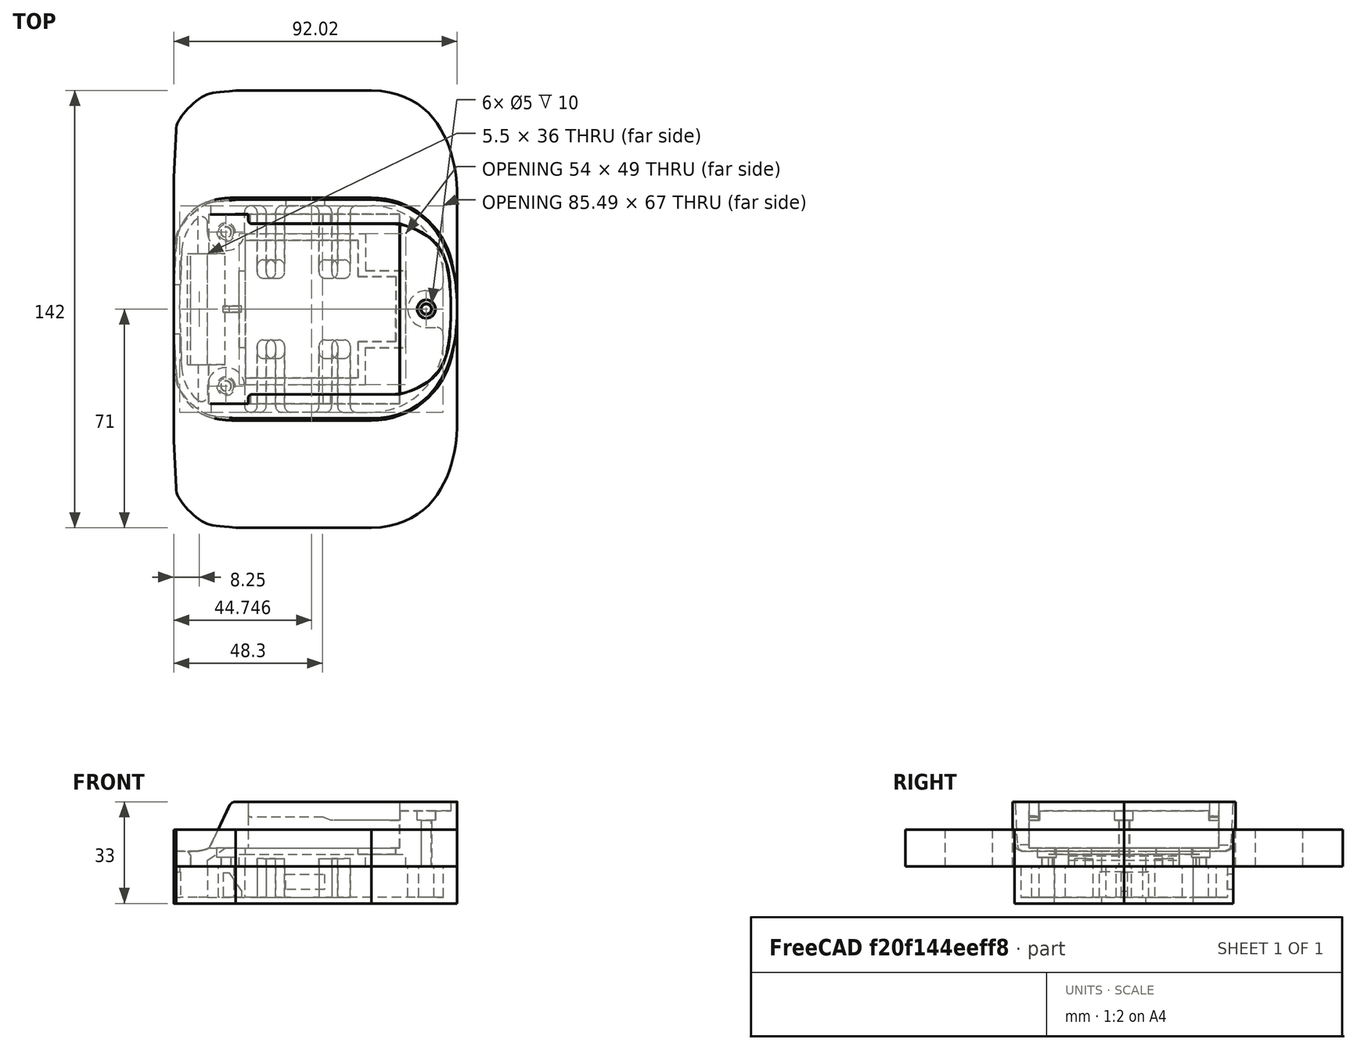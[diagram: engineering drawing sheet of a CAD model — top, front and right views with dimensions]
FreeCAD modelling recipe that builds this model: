
FCSTD DOCUMENT  (FreeCAD 1.0R39319 (Git))
Label: Makita LXT  - 18V - Battery holder
License: Creative Commons Attribution 4.0
LicenseURL: https://creativecommons.org/licenses/by/4.0/
objects: Sketcher::SketchObject×30, PartDesign::Pocket×23, TechDraw::DrawViewDimension×9, PartDesign::Pad×7, PartDesign::Body×5, TechDraw::DrawProjGroupItem×3, PartDesign::Mirrored×3, TechDraw::DrawSVGTemplate×2, TechDraw::DrawPage×2, Mesh::Feature×1, Part::Feature×1, TechDraw::DrawProjGroup×1
note: 180 computed .brp shape members not serialized (recipe doc carries the construction recipe); baked Part::Feature solids carry a one-line shape summary decoded from their .brp

FEATURE [Sketcher::SketchObject] Sketch
  ArcFitTolerance = 0
  AttachmentSupport = -> [XY_Plane]
  FullyConstrained = false
  MakeInternals = false
  MapMode = 5
  sketch-geometry (26):
    g0: ArcOfCircle CenterX=259.65 CenterY=-2.5774e-06 CenterZ=0 NormalX=0 NormalY=0 NormalZ=1 AngleXU=0 Radius=259.65 StartAngle=3.05831 EndAngle=3.14159
    g1: ArcOfCircle CenterX=16.3351 CenterY=20.3115 CenterZ=0 NormalX=0 NormalY=0 NormalZ=1 AngleXU=0 Radius=15.4888 StartAngle=1.76803 EndAngle=3.05831
    g2: LineSegment StartX=20 StartY=36.1629 StartZ=0 EndX=64.2 EndY=36.1629 EndZ=0
    g3: ArcOfCircle CenterX=64.2 CenterY=9.3939 CenterZ=0 NormalX=0 NormalY=0 NormalZ=1 AngleXU=0 Radius=26.769 StartAngle=0.218634 EndAngle=1.5708
    g4: ArcOfCircle CenterX=21.9206 CenterY=0 CenterZ=0 NormalX=0 NormalY=0 NormalZ=1 AngleXU=0 Radius=70.0794 StartAngle=0 EndAngle=0.218634
    g5: ArcOfCircle CenterX=20 CenterY=1.97116 CenterZ=0 NormalX=0 NormalY=0 NormalZ=1 AngleXU=0 Radius=34.1917 StartAngle=1.5708 EndAngle=1.76803
    g6: Circle CenterX=17 CenterY=25 CenterZ=0 NormalX=0 NormalY=0 NormalZ=1 AngleXU=0 Radius=1.6
    g7: ArcOfCircle CenterX=82 CenterY=0 CenterZ=0 NormalX=0 NormalY=0 NormalZ=1 AngleXU=0 Radius=1.6 StartAngle=0 EndAngle=3.14159
    g8: LineSegment StartX=23.3 StartY=0 StartZ=0 EndX=23.3 EndY=22.4 EndZ=0
    g9: LineSegment StartX=23.3 StartY=22.4 StartZ=0 EndX=59.9 EndY=22.4 EndZ=0
    g10: LineSegment StartX=59.9 StartY=22.4 StartZ=0 EndX=59.9 EndY=10.5 EndZ=0
    g11: LineSegment StartX=59.9 StartY=10.5 StartZ=0 EndX=72.1 EndY=10.5 EndZ=0
    g12: LineSegment StartX=72.1 StartY=10.5 StartZ=0 EndX=72.1 EndY=0 EndZ=0
    g13: ArcOfCircle CenterX=259.65 CenterY=2.5774e-06 CenterZ=0 NormalX=0 NormalY=0 NormalZ=1 AngleXU=0 Radius=259.65 StartAngle=3.14159 EndAngle=3.22488
    g14: ArcOfCircle CenterX=16.3351 CenterY=-20.3115 CenterZ=0 NormalX=0 NormalY=0 NormalZ=1 AngleXU=0 Radius=15.4888 StartAngle=3.22488 EndAngle=4.51516
    g15: LineSegment StartX=20 StartY=-36.1629 StartZ=0 EndX=64.2 EndY=-36.1629 EndZ=0
    g16: ArcOfCircle CenterX=64.2 CenterY=-9.3939 CenterZ=0 NormalX=0 NormalY=0 NormalZ=1 AngleXU=0 Radius=26.769 StartAngle=4.71239 EndAngle=6.06455
    g17: ArcOfCircle CenterX=21.9206 CenterY=0 CenterZ=0 NormalX=0 NormalY=0 NormalZ=1 AngleXU=0 Radius=70.0794 StartAngle=6.06455 EndAngle=6.28319
    g18: ArcOfCircle CenterX=20 CenterY=-1.97116 CenterZ=0 NormalX=0 NormalY=0 NormalZ=1 AngleXU=0 Radius=34.1917 StartAngle=4.51516 EndAngle=4.71239
    g19: Circle CenterX=17 CenterY=-25 CenterZ=0 NormalX=0 NormalY=0 NormalZ=1 AngleXU=0 Radius=1.6
    g20: ArcOfCircle CenterX=82 CenterY=0 CenterZ=0 NormalX=0 NormalY=0 NormalZ=1 AngleXU=0 Radius=1.6 StartAngle=3.14159 EndAngle=6.28319
    g21: LineSegment StartX=23.3 StartY=0 StartZ=0 EndX=23.3 EndY=-22.4 EndZ=0
    g22: LineSegment StartX=23.3 StartY=-22.4 StartZ=0 EndX=59.9 EndY=-22.4 EndZ=0
    g23: LineSegment StartX=59.9 StartY=-22.4 StartZ=0 EndX=59.9 EndY=-10.5 EndZ=0
    g24: LineSegment StartX=59.9 StartY=-10.5 StartZ=0 EndX=72.1 EndY=-10.5 EndZ=0
    g25: LineSegment StartX=72.1 StartY=-10.5 StartZ=0 EndX=72.1 EndY=0 EndZ=0
  constraints (64):
    c: Horizontal(g2)
    c: DistanceX(g2) = 20
    c: DistanceX(g2,g2) = 44.2
    c: Tangent(g4,g3) = -1.5708
    c: Tangent(g3,g2) = 1.5708
    c: Tangent(g1,g0) = -1.5708
    c: Tangent(g5,g2) = 1.5708
    c: Tangent(g5,g1) = -1.5708
    c: DistanceX(g0) = 0.9
    c: DistanceX(g1) = 13.3
    c: DistanceX(g4) = 92
    c: Coincident(g0,g-1)
    c: DistanceY(g0) = 21.6
    c: DistanceY(g1) = 35.5
    c: PointOnObject(g4,g-1)
    c: DistanceY(g3) = 15.2
    c: DistanceY(g6) = 25
    c: DistanceX(g6) = 17
    c: Diameter(g6) = 3.2
    c: PointOnObject(g7,g-1)
    c: PointOnObject(g7,g-1)
    c: PointOnObject(g7,g-1)
    c: DistanceX(g6,g7) = 65
    c: Equal(g7,g6)
    c: Tangent(g0,g-2)
    c: Perpendicular(g4,g-1)
    c: PointOnObject(g8,g-1)
    c: Vertical(g8)
    c: Coincident(g8,g9)
    c: Horizontal(g9)
    c: Coincident(g9,g10)
    c: Vertical(g10)
    c: Coincident(g10,g11)
    c: Horizontal(g11)
    c: Coincident(g11,g12)
    c: Vertical(g12)
    c: DistanceX(g8) = 23.3
    c: DistanceY(g8) = 22.4
    c: DistanceX(g9,g9) = 36.6
    c: DistanceY(g10,g10) = 11.9
    c: DistanceX(g11,g11) = 12.2
    c: PointOnObject(g12,g-1)
    c: Horizontal(g15)
    c: Tangent(g17,g16) = -1.5708
    c: Tangent(g16,g15) = -1.5708
    c: Tangent(g14,g13) = -1.5708
    c: Tangent(g18,g15) = -1.5708
    c: Tangent(g18,g14) = -1.5708
    c: Diameter(g19) = 3.2
    c: Equal(g20,g19)
    c: Vertical(g21)
    c: Coincident(g21,g22)
    c: Horizontal(g22)
    c: Coincident(g22,g23)
    c: Vertical(g23)
    c: Coincident(g23,g24)
    c: Horizontal(g24)
    c: Coincident(g24,g25)
    c: Vertical(g25)
    c: DistanceY(g15,g2) = 72.3257
    c: DistanceY(g19,g6) = 50
    c: DistanceX(g6,g7) = 66.6
    c: DistanceX(g6) = 17
    c: DistanceX(g4) = 92
FEATURE [Mesh::Feature] Makita_18V_Body  label="Makita 18V-Body"
  Placement = pos=(17,0,0) rot=(0,0,1;0rad)
FEATURE [PartDesign::Pad] Pad
  Direction = (0,0,1)
  Length = 21
  Length2 = 10
  Profile = -> Sketch
  ReferenceAxis = -> Sketch [N_Axis]
  Suppressed = false
  Type = 0
FEATURE [Sketcher::SketchObject] Sketch001
  ArcFitTolerance = 0
  AttachmentSupport = -> [XZ_Plane]
  FullyConstrained = true
  MakeInternals = false
  MapMode = 5
  Placement = pos=(0,0,0) rot=(1,0,0;1.5708rad)
  sketch-geometry (8):
    g0: LineSegment StartX=0 StartY=5 StartZ=0 EndX=0 EndY=21 EndZ=0
    g1: LineSegment StartX=0 StartY=21 StartZ=0 EndX=20 EndY=21 EndZ=0
    g2: LineSegment StartX=0 StartY=5 StartZ=0 EndX=7.9 EndY=5 EndZ=0
    g3: LineSegment StartX=18.2 StartY=19.8659 StartZ=0 EndX=11.9 EndY=6.7 EndZ=0
    g4: ArcOfCircle CenterX=20 CenterY=19.0045 CenterZ=0 NormalX=0 NormalY=0 NormalZ=1 AngleXU=0 Radius=1.99546 StartAngle=1.5708 EndAngle=2.69528
    g5: ArcOfCircle CenterX=10.0257 CenterY=7.59685 CenterZ=0 NormalX=0 NormalY=0 NormalZ=1 AngleXU=0 Radius=2.07779 StartAngle=4.99242 EndAngle=5.83688
    g6: ArcOfCircle CenterX=7.9 CenterY=5.60003 CenterZ=0 NormalX=0 NormalY=0 NormalZ=1 AngleXU=0 Radius=0.600034 StartAngle=4.71239 EndAngle=4.87983
    g7: ArcOfCircle CenterX=4.0509 CenterY=28.3729 CenterZ=0 NormalX=0 NormalY=0 NormalZ=1 AngleXU=0 Radius=23.6959 StartAngle=4.87983 EndAngle=4.99242
  constraints (22):
    c: PointOnObject(g0,g-2)
    c: PointOnObject(g0,g-2)
    c: Horizontal(g1)
    c: Coincident(g1,g0)
    c: DistanceY(g0) = 5
    c: DistanceY(g0) = 21
    c: Coincident(g2,g0)
    c: Horizontal(g2)
    c: Tangent(g4,g3) = -1.5708
    c: Tangent(g5,g3) = 1.5708
    c: Tangent(g4,g1) = 1.5708
    c: DistanceX(g1,g1) = 20
    c: DistanceX(g3) = 11.9
    c: DistanceY(g3) = 6.7
    c: DistanceX(g3) = 18.2
    c: Tangent(g6,g2) = -1.5708
    c: DistanceX(g2,g2) = 7.9
    c: Tangent(g7,g5) = -1.5708
    c: Tangent(g7,g6) = -1.5708
    c: DistanceX(g2,g6) = 0.1
    c: DistanceX(g5) = 10.6
    c: DistanceY(g5) = 5.6
FEATURE [PartDesign::Pocket] Pocket
  BaseFeature = -> Pad
  Direction = (0,1,-2e-16)
  Length = 5
  Length2 = 5
  Midplane = true
  Profile = -> Sketch001
  ReferenceAxis = -> Sketch001 [N_Axis]
  Suppressed = false
  Type = 1
FEATURE [Part::Feature] Makita_18V_Body001
  shape: bbox 92 x 71 x 21 mm, 5406 faces, 0 solids (baked)
FEATURE [Sketcher::SketchObject] Sketch002
  ArcFitTolerance = 0
  AttachmentSupport = -> [Pocket]
  FullyConstrained = false
  MakeInternals = false
  MapMode = 5
  Placement = pos=(0,0,21) rot=(0,0,1;0rad)
  sketch-geometry (16):
    g0: LineSegment StartX=24.2 StartY=30.78 StartZ=0 EndX=0 EndY=30.78 EndZ=0
    g1: LineSegment StartX=24.2 StartY=30.78 StartZ=0 EndX=24.2 EndY=28.88 EndZ=0
    g2: LineSegment StartX=25.4 StartY=27.68 StartZ=0 EndX=70.2 EndY=27.68 EndZ=0
    g3: ArcOfCircle CenterX=25.4 CenterY=28.88 CenterZ=0 NormalX=0 NormalY=0 NormalZ=1 AngleXU=0 Radius=1.2 StartAngle=3.14159 EndAngle=4.71239
    g4: ArcOfCircle CenterX=15.7361 CenterY=0 CenterZ=0 NormalX=0 NormalY=0 NormalZ=1 AngleXU=0 Radius=74.2639 StartAngle=0 EndAngle=0.199259
    g5: ArcOfCircle CenterX=74.666 CenterY=11.9002 CenterZ=0 NormalX=0 NormalY=0 NormalZ=1 AngleXU=0 Radius=14.1444 StartAngle=0.199259 EndAngle=0.868771
    g6: ArcOfCircle CenterX=70.2 CenterY=6.61972 CenterZ=0 NormalX=0 NormalY=0 NormalZ=1 AngleXU=0 Radius=21.0603 StartAngle=0.868771 EndAngle=1.5708
    g7: LineSegment StartX=0 StartY=0 StartZ=0 EndX=0 EndY=30.78 EndZ=0
    g8: LineSegment StartX=24.2 StartY=-30.78 StartZ=0 EndX=0 EndY=-30.78 EndZ=0
    g9: LineSegment StartX=24.2 StartY=-30.78 StartZ=0 EndX=24.2 EndY=-28.88 EndZ=0
    g10: LineSegment StartX=25.4 StartY=-27.68 StartZ=0 EndX=70.2 EndY=-27.68 EndZ=0
    g11: ArcOfCircle CenterX=25.4 CenterY=-28.88 CenterZ=0 NormalX=0 NormalY=0 NormalZ=1 AngleXU=0 Radius=1.2 StartAngle=1.5708 EndAngle=3.14159
    g12: ArcOfCircle CenterX=15.7361 CenterY=0 CenterZ=0 NormalX=0 NormalY=0 NormalZ=1 AngleXU=0 Radius=74.2639 StartAngle=6.08393 EndAngle=6.28319
    g13: ArcOfCircle CenterX=74.666 CenterY=-11.9002 CenterZ=0 NormalX=0 NormalY=0 NormalZ=1 AngleXU=0 Radius=14.1444 StartAngle=5.41441 EndAngle=6.08393
    g14: ArcOfCircle CenterX=70.2 CenterY=-6.61972 CenterZ=0 NormalX=0 NormalY=0 NormalZ=1 AngleXU=0 Radius=21.0603 StartAngle=4.71239 EndAngle=5.41441
    g15: LineSegment StartX=0 StartY=0 StartZ=0 EndX=0 EndY=-30.78 EndZ=0
  constraints (36):
    c: PointOnObject(g0,g-2)
    c: Horizontal(g0)
    c: DistanceY(g0) = 30.78
    c: DistanceX(g0,g0) = 24.2
    c: Coincident(g1,g0)
    c: Vertical(g1)
    c: Horizontal(g2)
    c: Tangent(g3,g1) = -1.5708
    c: Tangent(g3,g2) = -1.5708
    c: DistanceY(g1,g1) = 1.9
    c: Radius(g3) = 1.2
    c: PointOnObject(g4,g-1)
    c: Perpendicular(g4,g-1)
    c: DistanceX(g4) = 90
    c: DistanceY(g4) = 14.7
    c: Tangent(g6,g5) = -1.5708
    c: Tangent(g5,g4) = -1.5708
    c: Tangent(g6,g2) = 1.5708
    c: DistanceX(g2,g2) = 44.8
    c: DistanceX(g5) = 83.8
    c: DistanceY(g5) = 22.7
    c: PointOnObject(g7,g-1)
    c: Coincident(g7,g0)
    c: Vertical(g7)
    c: Horizontal(g8)
    c: Coincident(g9,g8)
    c: Vertical(g9)
    c: Horizontal(g10)
    c: Tangent(g11,g9) = 1.5708
    c: Tangent(g11,g10) = 1.5708
    c: Radius(g11) = 1.2
    c: Tangent(g14,g13) = -1.5708
    c: Tangent(g13,g12) = -1.5708
    c: Tangent(g14,g10) = -1.5708
    c: Coincident(g15,g8)
    c: Vertical(g15)
FEATURE [PartDesign::Pocket] Pocket001
  BaseFeature = -> Pocket
  Direction = (0,0,-1)
  Length = 3
  Length2 = 5
  Profile = -> Sketch002
  ReferenceAxis = -> Sketch002 [N_Axis]
  Suppressed = false
  Type = 0
FEATURE [Sketcher::SketchObject] Sketch003
  ArcFitTolerance = 0
  AttachmentSupport = -> [Pocket001]
  ExternalGeometry = -> [Sketch002]
  FullyConstrained = false
  MakeInternals = false
  MapMode = 5
  Placement = pos=(0,0,18) rot=(0,0,1;0rad)
  sketch-geometry (14):
    g0: LineSegment StartX=0 StartY=0 StartZ=0 EndX=0 EndY=30.78 EndZ=0
    g1: LineSegment StartX=0 StartY=30.78 StartZ=0 EndX=24.2 EndY=30.78 EndZ=0
    g2: LineSegment StartX=24.2 StartY=28.88 StartZ=0 EndX=24.2 EndY=30.78 EndZ=0
    g3: LineSegment StartX=25.4 StartY=27.68 StartZ=0 EndX=70.2 EndY=27.68 EndZ=0
    g4: ArcOfCircle CenterX=25.4 CenterY=28.88 CenterZ=0 NormalX=0 NormalY=0 NormalZ=1 AngleXU=0 Radius=1.2 StartAngle=3.14159 EndAngle=4.71239
    g5: LineSegment StartX=73.4 StartY=27.4355 StartZ=0 EndX=73.4 EndY=0 EndZ=0
    g6: ArcOfCircle CenterX=70.2 CenterY=6.61972 CenterZ=0 NormalX=0 NormalY=0 NormalZ=1 AngleXU=0 Radius=21.0603 StartAngle=1.41826 EndAngle=1.5708
    g7: LineSegment StartX=0 StartY=0 StartZ=0 EndX=0 EndY=-30.78 EndZ=0
    g8: LineSegment StartX=0 StartY=-30.78 StartZ=0 EndX=24.2 EndY=-30.78 EndZ=0
    g9: LineSegment StartX=24.2 StartY=-28.88 StartZ=0 EndX=24.2 EndY=-30.78 EndZ=0
    g10: LineSegment StartX=25.4 StartY=-27.68 StartZ=0 EndX=70.2 EndY=-27.68 EndZ=0
    g11: ArcOfCircle CenterX=25.4 CenterY=-28.88 CenterZ=0 NormalX=0 NormalY=0 NormalZ=1 AngleXU=0 Radius=1.2 StartAngle=1.5708 EndAngle=3.14159
    g12: LineSegment StartX=73.4 StartY=-27.4355 StartZ=0 EndX=73.4 EndY=0 EndZ=0
    g13: ArcOfCircle CenterX=70.2 CenterY=-6.61972 CenterZ=0 NormalX=0 NormalY=0 NormalZ=1 AngleXU=0 Radius=21.0603 StartAngle=4.71239 EndAngle=4.86492
  constraints (23):
    c: Coincident(g0,g-3)
    c: Coincident(g0,g-4)
    c: Coincident(g1,g0)
    c: Coincident(g1,g-4)
    c: Coincident(g2,g-7)
    c: Coincident(g2,g1)
    c: Coincident(g3,g-5)
    c: Coincident(g3,g-6)
    c: Coincident(g4,g2)
    c: Tangent(g4,g3) = -1.5708
    c: PointOnObject(g5,g-6)
    c: PointOnObject(g5,g-1)
    c: Vertical(g5)
    c: Coincident(g6,g5)
    c: Tangent(g6,g3) = 1.5708
    c: DistanceX(g5) = 73.4
    c: Coincident(g8,g7)
    c: Coincident(g9,g8)
    c: Coincident(g11,g9)
    c: Tangent(g11,g10) = 1.5708
    c: Vertical(g12)
    c: Coincident(g13,g12)
    c: Tangent(g13,g10) = -1.5708
FEATURE [PartDesign::Pocket] Pocket002
  BaseFeature = -> Pocket001
  Direction = (0,0,-1)
  Length = 12
  Length2 = 5
  Profile = -> Sketch003
  ReferenceAxis = -> Sketch003 [N_Axis]
  Suppressed = false
  Type = 0
FEATURE [Sketcher::SketchObject] Sketch004
  ArcFitTolerance = 0
  AttachmentSupport = -> [Pocket002]
  ExternalGeometry = -> [Pocket002]
  FullyConstrained = true
  MakeInternals = false
  MapMode = 5
  Placement = pos=(0,0,6) rot=(0,0,1;0rad)
  sketch-geometry (2):
    g0: Circle CenterX=17 CenterY=25 CenterZ=0 NormalX=0 NormalY=0 NormalZ=1 AngleXU=0 Radius=3
    g1: Circle CenterX=17 CenterY=-25 CenterZ=0 NormalX=0 NormalY=0 NormalZ=1 AngleXU=0 Radius=3
  constraints (4):
    c: Symmetric(g1,g0,g-1)
    c: Equal(g0,g1)
    c: Coincident(g-3,g0)
    c: Diameter(g0) = 6
FEATURE [PartDesign::Pocket] Pocket003
  BaseFeature = -> Pocket002
  Direction = (0,0,-1)
  Length = 3
  Length2 = 5
  Profile = -> Sketch004
  ReferenceAxis = -> Sketch004 [N_Axis]
  Suppressed = false
  Type = 0
FEATURE [Sketcher::SketchObject] Sketch005
  ArcFitTolerance = 0
  AttachmentSupport = -> [Pocket003]
  ExternalGeometry = -> [Pocket003]
  FullyConstrained = true
  MakeInternals = false
  MapMode = 5
  Placement = pos=(0,0,18) rot=(0,0,1;0rad)
  sketch-geometry (1):
    g0: Circle CenterX=82 CenterY=0 CenterZ=0 NormalX=0 NormalY=0 NormalZ=1 AngleXU=0 Radius=3
  constraints (2):
    c: Coincident(g0,g-3)
    c: Diameter(g0) = 6
FEATURE [PartDesign::Pocket] Pocket004
  BaseFeature = -> Pocket003
  Direction = (0,0,-1)
  Length = 3
  Length2 = 5
  Profile = -> Sketch005
  ReferenceAxis = -> Sketch005 [N_Axis]
  Suppressed = false
  Type = 0
FEATURE [Sketcher::SketchObject] Sketch006
  ArcFitTolerance = 0
  AttachmentSupport = -> [XZ_Plane]
  ExternalGeometry = -> [Sketch003]
  FullyConstrained = true
  MakeInternals = false
  MapMode = 5
  Placement = pos=(0,0,0) rot=(1,0,0;1.5708rad)
  sketch-geometry (7):
    g0: LineSegment StartX=73.4 StartY=15 StartZ=0 EndX=51 EndY=15 EndZ=0
    g1: LineSegment StartX=51 StartY=15 StartZ=0 EndX=48.5 EndY=16 EndZ=0
    g2: LineSegment StartX=48.5 StartY=16 StartZ=0 EndX=25 EndY=16 EndZ=0
    g3: LineSegment StartX=24.2 StartY=16.4 StartZ=0 EndX=25 EndY=16 EndZ=0
    g4: LineSegment StartX=24.2 StartY=16.4 StartZ=0 EndX=24.2 EndY=6 EndZ=0
    g5: LineSegment StartX=24.2 StartY=6 StartZ=0 EndX=73.4 EndY=6 EndZ=0
    g6: LineSegment StartX=73.4 StartY=6 StartZ=0 EndX=73.4 EndY=15 EndZ=0
  constraints (21):
    c: Horizontal(g0)
    c: Coincident(g1,g0)
    c: Coincident(g2,g1)
    c: Horizontal(g2)
    c: Coincident(g2,g3)
    c: Coincident(g4,g3)
    c: Vertical(g4)
    c: Coincident(g5,g4)
    c: Horizontal(g5)
    c: Coincident(g6,g5)
    c: Coincident(g6,g0)
    c: Vertical(g6)
    c: Vertical(g0,g-3)
    c: Vertical(g3,g-5)
    c: DistanceY(g4) = 6
    c: DistanceY(g4,g4) = 10.4
    c: DistanceY(g2) = 16
    c: DistanceX(g3,g2) = 0.8
    c: DistanceX(g2,g2) = 23.5
    c: DistanceY(g0) = 15
    c: DistanceX(g1,g0) = 2.5
FEATURE [PartDesign::Pocket] Pocket005
  BaseFeature = -> Pocket004
  Direction = (0,1,-2e-16)
  Length = 61.6
  Length2 = 5
  Midplane = true
  Profile = -> Sketch006
  ReferenceAxis = -> Sketch006 [N_Axis]
  Suppressed = false
  Type = 0
FEATURE [Sketcher::SketchObject] Sketch007
  ArcFitTolerance = 0
  AttachmentSupport = -> [Pocket005]
  ExternalGeometry = -> [Pocket005]
  FullyConstrained = false
  MakeInternals = false
  MapMode = 5
  Placement = pos=(0,0,0) rot=(1,0,0;3.14159rad)
  sketch-geometry (14):
    g0: LineSegment StartX=21.3 StartY=0 StartZ=0 EndX=21.3 EndY=12.5 EndZ=0
    g1: LineSegment StartX=21.3 StartY=12.5 StartZ=0 EndX=23.3 EndY=12.5 EndZ=0
    g2: LineSegment StartX=23.3 StartY=12.5 StartZ=0 EndX=23.3 EndY=24.5 EndZ=0
    g3: LineSegment StartX=23.3 StartY=24.5 StartZ=0 EndX=62.3 EndY=24.5 EndZ=0
    g4: LineSegment StartX=62.3 StartY=24.5 StartZ=0 EndX=62.3 EndY=12.5 EndZ=0
    g5: LineSegment StartX=62.3 StartY=12.5 StartZ=0 EndX=75.3 EndY=12.5 EndZ=0
    g6: LineSegment StartX=75.3 StartY=12.5 StartZ=0 EndX=75.3 EndY=0 EndZ=0
    g7: LineSegment StartX=21.3 StartY=0 StartZ=0 EndX=21.3 EndY=-12.5 EndZ=0
    g8: LineSegment StartX=21.3 StartY=-12.5 StartZ=0 EndX=23.3 EndY=-12.5 EndZ=0
    g9: LineSegment StartX=23.3 StartY=-12.5 StartZ=0 EndX=23.3 EndY=-24.5 EndZ=0
    g10: LineSegment StartX=23.3 StartY=-24.5 StartZ=0 EndX=62.3 EndY=-24.5 EndZ=0
    g11: LineSegment StartX=62.3 StartY=-24.5 StartZ=0 EndX=62.3 EndY=-12.5 EndZ=0
    g12: LineSegment StartX=62.3 StartY=-12.5 StartZ=0 EndX=75.3 EndY=-12.5 EndZ=0
    g13: LineSegment StartX=75.3 StartY=-12.5 StartZ=0 EndX=75.3 EndY=0 EndZ=0
  constraints (35):
    c: PointOnObject(g0,g-1)
    c: Vertical(g0)
    c: Coincident(g0,g1)
    c: PointOnObject(g1,g-3)
    c: Horizontal(g1)
    c: Coincident(g1,g2)
    c: Vertical(g2)
    c: Coincident(g2,g3)
    c: Horizontal(g3)
    c: Coincident(g3,g4)
    c: Vertical(g4)
    c: Coincident(g4,g5)
    c: Horizontal(g5)
    c: Coincident(g5,g6)
    c: PointOnObject(g6,g-1)
    c: Vertical(g6)
    c: DistanceY(g2) = 24.5
    c: DistanceY(g0,g0) = 12.5
    c: DistanceX(g1,g1) = 2
    c: DistanceX(g-4,g3) = 2.4
    c: DistanceY(g-5,g4) = 2
    c: DistanceX(g-5,g5) = 3.2
    c: Vertical(g7)
    c: Coincident(g7,g8)
    c: Horizontal(g8)
    c: Coincident(g8,g9)
    c: Vertical(g9)
    c: Coincident(g9,g10)
    c: Horizontal(g10)
    c: Coincident(g10,g11)
    c: Vertical(g11)
    c: Coincident(g11,g12)
    c: Horizontal(g12)
    c: Coincident(g12,g13)
    c: Vertical(g13)
FEATURE [PartDesign::Pocket] Pocket006
  BaseFeature = -> Pocket005
  Direction = (0,0,1)
  Length = 4
  Length2 = 5
  Profile = -> Sketch007
  ReferenceAxis = -> Sketch007 [N_Axis]
  Suppressed = false
  Type = 0
FEATURE [Sketcher::SketchObject] Sketch008
  ArcFitTolerance = 0
  AttachmentSupport = -> [XZ_Plane]
  FullyConstrained = true
  MakeInternals = false
  MapMode = 5
  Placement = pos=(0,0,0) rot=(1,0,0;1.5708rad)
  sketch-geometry (7):
    g0: LineSegment StartX=5.5 StartY=0 StartZ=0 EndX=11 EndY=0 EndZ=0
    g1: LineSegment StartX=11 StartY=0 StartZ=0 EndX=11 EndY=2 EndZ=0
    g2: LineSegment StartX=11 StartY=2 StartZ=0 EndX=16.7 EndY=6 EndZ=0
    g3: LineSegment StartX=16.7 StartY=6 StartZ=0 EndX=4.45 EndY=6 EndZ=0
    g4: LineSegment StartX=4.45 StartY=6 StartZ=0 EndX=4.45 EndY=5 EndZ=0
    g5: LineSegment StartX=4.45 StartY=5 StartZ=0 EndX=5.5 EndY=3.5 EndZ=0
    g6: LineSegment StartX=5.5 StartY=3.5 StartZ=0 EndX=5.5 EndY=0 EndZ=0
  constraints (21):
    c: PointOnObject(g0,g-1)
    c: PointOnObject(g0,g-1)
    c: Coincident(g0,g1)
    c: Vertical(g1)
    c: Coincident(g1,g2)
    c: Coincident(g2,g3)
    c: Horizontal(g3)
    c: Coincident(g3,g4)
    c: Vertical(g4)
    c: Coincident(g4,g5)
    c: Coincident(g5,g6)
    c: Coincident(g6,g0)
    c: Vertical(g6)
    c: DistanceX(g0) = 5.5
    c: DistanceX(g0) = 11
    c: DistanceY(g6,g6) = 3.5
    c: DistanceY(g1,g1) = 2
    c: DistanceY(g2) = 6
    c: DistanceX(g2) = 16.7
    c: DistanceY(g4) = 5
    c: DistanceX(g4) = 4.45
FEATURE [PartDesign::Pocket] Pocket007
  BaseFeature = -> Pocket006
  Direction = (0,1,-2e-16)
  Length = 36
  Length2 = 5
  Midplane = true
  Profile = -> Sketch008
  ReferenceAxis = -> Sketch008 [N_Axis]
  Suppressed = false
  Type = 0
FEATURE [PartDesign::Body] Body  label="Battery mount"
  AllowCompound = false
  Group = -> [Sketch,Pad,Sketch001,Pocket,Sketch002,Pocket001,Sketch003,Pocket002,Sketch004,Pocket003,Sketch005,Pocket004,Sketch006,Pocket005,Sketch007,Pocket006,Sketch008,Pocket007]
  Origin = -> Origin
  Tip = -> Pocket007
FEATURE [TechDraw::DrawSVGTemplate] Template
  EditableTexts = approval_person=B. Hecate; creator=Jon Sagebrand; date_of_issue=2026-02-17; document_type=Component Drawing; general_tolerances=ISO 2768-m; identification_number=DN; language_code=EN; legal_owner_1=Jonix; part_material=Stainless steel Mat.No. 1.4301; revision_index=AAA; scale=1 : 1; sheet_number=1 / 1; title=Makita LXT  - 18V - Battery holder
  Height = 210
  Orientation = 1
  Template = <path>
  Width = 297
FEATURE [TechDraw::DrawProjGroupItem] View
  CoarseView = false
  Direction = (0,0,-1)
  Focus = 100
  HardHidden = false
  IsoCount = 0
  IsoHidden = false
  IsoVisible = false
  LockPosition = false
  Perspective = false
  Rotation = 0
  RotationVector = (1,0,0)
  ScaleType = 0
  ScrubCount = 1
  SeamHidden = false
  SeamVisible = false
  SmoothHidden = false
  SmoothVisible = true
  Source = -> [Pocket007]
  Type = 0
  X = 157.417
  XDirection = (1,0,0)
  Y = 121.596
FEATURE [TechDraw::DrawViewDimension] Dimension
  AngleOverride = false
  Arbitrary = false
  ArbitraryTolerances = false
  BoxCorners = (2) [(-46,-36.1629,0),(46,36.1629,0)]
  EqualTolerance = true
  ExtensionAngle = 0
  FormatSpec = %.2w
  FormatSpecOverTolerance = %+.2w
  FormatSpecUnderTolerance = %+.2w
  Inverted = false
  LineAngle = 0
  LockPosition = false
  MeasureType = 1
  OverTolerance = 0
  References2D = -> [View]
  Rotation = 0
  ScaleType = 0
  TheoreticalExact = false
  Type = 2
  UnderTolerance = 0
  X = -60.9397
  Y = 3.59505
FEATURE [TechDraw::DrawViewDimension] Dimension001
  AngleOverride = false
  Arbitrary = false
  ArbitraryTolerances = false
  BoxCorners = (2) [(-46,-36.1629,0),(46,36.1629,0)]
  EqualTolerance = true
  ExtensionAngle = 0
  FormatSpec = %.2w
  FormatSpecOverTolerance = %+.2w
  FormatSpecUnderTolerance = %+.2w
  Inverted = false
  LineAngle = 0
  LockPosition = false
  MeasureType = 1
  OverTolerance = 0
  References2D = -> [View]
  Rotation = 0
  ScaleType = 0
  TheoreticalExact = false
  Type = 2
  UnderTolerance = 0
  X = -74.0234
  Y = 0
FEATURE [TechDraw::DrawViewDimension] Dimension002
  AngleOverride = false
  Arbitrary = false
  ArbitraryTolerances = false
  BoxCorners = (2) [(-46,-36.1629,0),(46,36.1629,0)]
  EqualTolerance = true
  ExtensionAngle = 0
  FormatSpec = %.2w
  FormatSpecOverTolerance = %+.2w
  FormatSpecUnderTolerance = %+.2w
  Inverted = false
  LineAngle = 0
  LockPosition = false
  MeasureType = 1
  OverTolerance = 0
  References2D = -> [View]
  Rotation = 0
  ScaleType = 0
  TheoreticalExact = false
  Type = 1
  UnderTolerance = 0
  X = 3.5
  Y = 57.7106
FEATURE [TechDraw::DrawViewDimension] Dimension003
  AngleOverride = false
  Arbitrary = false
  ArbitraryTolerances = false
  BoxCorners = (2) [(-46,-36.1629,0),(46,36.1629,0)]
  EqualTolerance = true
  ExtensionAngle = 0
  FormatSpec = %.2w
  FormatSpecOverTolerance = %+.2w
  FormatSpecUnderTolerance = %+.2w
  Inverted = false
  LineAngle = 0
  LockPosition = false
  MeasureType = 1
  OverTolerance = 0
  References2D = -> [View]
  Rotation = 0
  ScaleType = 0
  TheoreticalExact = false
  Type = 1
  UnderTolerance = 0
  X = 0
  Y = -48.6903
FEATURE [TechDraw::DrawViewDimension] Dimension004
  AngleOverride = false
  Arbitrary = false
  ArbitraryTolerances = false
  BoxCorners = (2) [(-46,-36.1629,0),(46,36.1629,0)]
  EqualTolerance = true
  ExtensionAngle = 0
  FormatSpec = %.2w
  FormatSpecOverTolerance = %+.2w
  FormatSpecUnderTolerance = %+.2w
  Inverted = false
  LineAngle = 0
  LockPosition = false
  MeasureType = 1
  OverTolerance = 0
  References2D = -> [View]
  Rotation = 0
  ScaleType = 0
  TheoreticalExact = false
  Type = 1
  UnderTolerance = 0
  X = -37.5
  Y = 57.7106
FEATURE [TechDraw::DrawViewDimension] Dimension005
  AngleOverride = false
  Arbitrary = false
  ArbitraryTolerances = false
  BoxCorners = (2) [(-46,-36.1629,0),(46,36.1629,0)]
  EqualTolerance = true
  ExtensionAngle = 0
  FormatSpec = %.2w
  FormatSpecOverTolerance = %+.2w
  FormatSpecUnderTolerance = %+.2w
  Inverted = false
  LineAngle = 0
  LockPosition = false
  MeasureType = 1
  OverTolerance = 0
  References2D = -> [View]
  Rotation = 0
  ScaleType = 0
  TheoreticalExact = false
  Type = 1
  UnderTolerance = 0
  X = 41
  Y = 57.7106
FEATURE [TechDraw::DrawPage] Page
  KeepUpdated = true
  NextBalloonIndex = 1
  ProjectionType = 0
  Template = -> Template
  Views = -> [View,Dimension,Dimension001,Dimension002,Dimension003,Dimension004,Dimension005]
FEATURE [Sketcher::SketchObject] Sketch009
  ArcFitTolerance = 1e-06
  AttachmentSupport = -> [XY_Plane001]
  FullyConstrained = false
  MakeInternals = false
  MapMode = 5
  sketch-geometry (35):
    g0: LineSegment StartX=23.3 StartY=22.3 StartZ=0 EndX=59.9 EndY=22.3 EndZ=0
    g1: LineSegment StartX=59.9 StartY=22.3 StartZ=0 EndX=59.9 EndY=10.55 EndZ=0
    g2: LineSegment StartX=59.9 StartY=10.55 StartZ=0 EndX=72.15 EndY=10.55 EndZ=0
    g3: LineSegment StartX=72.15 StartY=10.55 StartZ=0 EndX=72.15 EndY=0 EndZ=0
    g4: LineSegment StartX=72.15 StartY=0 StartZ=0 EndX=80.25 EndY=2e-16 EndZ=0
    g5: LineSegment StartX=83.75 StartY=0 StartZ=0 EndX=92 EndY=0 EndZ=0
    g6: ArcOfCircle CenterX=82 CenterY=0 CenterZ=0 NormalX=0 NormalY=0 NormalZ=1 AngleXU=0 Radius=1.75 StartAngle=0 EndAngle=3.14159
    g7: LineSegment StartX=0 StartY=6.35e-14 StartZ=0 EndX=5.5 EndY=0 EndZ=0
    g8: LineSegment StartX=5.5 StartY=0 StartZ=0 EndX=5.5 EndY=18 EndZ=0
    g9: LineSegment StartX=5.5 StartY=18 StartZ=0 EndX=11 EndY=18 EndZ=0
    g10: LineSegment StartX=11 StartY=0 StartZ=0 EndX=23.3 EndY=0 EndZ=0
    g11: LineSegment StartX=0.05 StartY=7.2 StartZ=0 EndX=0.75 EndY=22.55 EndZ=0
    g12: ArcOfCircle CenterX=518.425 CenterY=0 CenterZ=0 NormalX=0 NormalY=0 NormalZ=1 AngleXU=0 Radius=518.425 StartAngle=3.1277 EndAngle=3.14159
    g13: LineSegment StartX=11 StartY=0 StartZ=0 EndX=11 EndY=18 EndZ=0
    g14: LineSegment StartX=20.1 StartY=35.5 StartZ=0 EndX=64.2 EndY=35.5 EndZ=0
    g15-g20: Circle [constr] x6 (B-spline internal-alignment scaffolding for g21; pole/knot coordinates omitted)
    g21: BSplineCurve PolesCount=6 KnotsCount=4 Degree=3 IsPeriodic=0
    g22-g25: GeomPoint [constr] x4 (B-spline internal-alignment scaffolding for g21; pole/knot coordinates omitted)
    g26-g29: Circle [constr] x4 (B-spline internal-alignment scaffolding for g30; pole/knot coordinates omitted)
    g30: BSplineCurve PolesCount=4 KnotsCount=2 Degree=3 IsPeriodic=0
    g31: GeomPoint [constr] X=92 Y=0 Z=0
    g32: GeomPoint [constr] X=64.2 Y=35.5 Z=0
    g33: Circle CenterX=17 CenterY=25 CenterZ=0 NormalX=0 NormalY=0 NormalZ=1 AngleXU=0 Radius=1.75
    g34: LineSegment StartX=23.3 StartY=0 StartZ=0 EndX=23.3 EndY=22.3 EndZ=0
  constraints (71):
    c: PointOnObject(g10,g-1)
    c: Horizontal(g0)
    c: Coincident(g0,g1)
    c: Vertical(g1)
    c: Coincident(g1,g2)
    c: Horizontal(g2)
    c: Coincident(g2,g3)
    c: PointOnObject(g3,g-1)
    c: Vertical(g3)
    c: Coincident(g4,g3)
    c: PointOnObject(g4,g-1)
    c: PointOnObject(g5,g-1)
    c: PointOnObject(g5,g-1)
    c: Coincident(g6,g4)
    c: Coincident(g6,g5)
    c: PointOnObject(g6,g-1)
    c: Coincident(g7,g-1)
    c: PointOnObject(g7,g-1)
    c: Coincident(g8,g7)
    c: Vertical(g8)
    c: Horizontal(g9)
    c: PointOnObject(g10,g-1)
    c: DistanceX(g7,g7) = 5.5
    c: DistanceX(g7,g10) = 5.5
    c: Coincident(g9,g8)
    c: DistanceY(g8,g8) = 18
    c: Diameter(g6) = 3.5
    c: DistanceX(g5,g5) = 8.25
    c: DistanceX(g5) = 92
    c: DistanceX(g11) = 0.75
    c: DistanceY(g11) = 22.55
    c: Coincident(g12,g7)
    c: Coincident(g12,g11)
    c: DistanceX(g11) = 0.05
    c: DistanceY(g11) = 7.2
    c: Perpendicular(g12,g-1)
    c: Radius(g12) = 518.425
    c: Coincident(g13,g10)
    c: Coincident(g13,g9)
    c: Vertical(g13)
    c: Horizontal(g14)
    c: DistanceY(g14) = 35.5
    c: DistanceX(g14) = 20.1
    c: DistanceX(g14,g14) = 44.1
    c: Weight(g15) = 1
    c: Equal(g15, g16-g20) x5
    c: InternalAlignment(g15-g20 -> g21) x6
    c: InternalAlignment(g22-g25 -> g21) x4
    c: Coincident(g15,g11)
    c: Coincident(g20,g14)
    c: Weight(g26) = 1
    c: Equal(g26,g27)
    c: Equal(g26,g28)
    c: Equal(g26,g29)
    c: InternalAlignment(g26-g29 -> g30) x4
    c: InternalAlignment(g31,g30)
    c: InternalAlignment(g32,g30)
    c: Coincident(g26,g5)
    c: Coincident(g29,g14)
    c: DistanceY(g33) = 25
    c: DistanceX(g33,g6) = 65
    c: Equal(g33,g6)
    c: Coincident(g34,g10)
    c: Coincident(g34,g0)
    c: Vertical(g34)
    c: DistanceX(g10,g10) = 12.3
    c: DistanceY(g34,g34) = 22.3
    c: DistanceX(g0,g0) = 36.6
    c: DistanceY(g1,g1) = 11.75
    c: DistanceX(g2,g2) = 12.25
    c: DistanceX(g4,g4) = 8.1
FEATURE [PartDesign::Pad] Pad001
  Direction = (0,0,1)
  Length = 21
  Length2 = 10
  Profile = -> Sketch009
  ReferenceAxis = -> Sketch009 [N_Axis]
  Refine = true
  Suppressed = false
  Type = 0
FEATURE [Sketcher::SketchObject] Sketch010
  ArcFitTolerance = 1e-06
  AttachmentSupport = -> [Pad001]
  ExternalGeometry = -> [Pad001]
  FullyConstrained = false
  MakeInternals = false
  MapMode = 5
  Placement = pos=(0,0,0) rot=(1,0,0;1.5708rad)
  sketch-geometry (14):
    g0: LineSegment StartX=7.9 StartY=5 StartZ=0 EndX=0 EndY=5 EndZ=0
    g1: LineSegment StartX=0 StartY=5 StartZ=0 EndX=0 EndY=21 EndZ=0
    g2: LineSegment StartX=0 StartY=21 StartZ=0 EndX=20.05 EndY=21 EndZ=0
    g3: LineSegment StartX=18.1059 StartY=19.7681 StartZ=0 EndX=12.1 EndY=7.05 EndZ=0
    g4: ArcOfCircle CenterX=20.05 CenterY=18.85 CenterZ=0 NormalX=0 NormalY=0 NormalZ=1 AngleXU=0 Radius=2.15 StartAngle=1.5708 EndAngle=2.70041
    g5-g9: Circle [constr] x5 (B-spline internal-alignment scaffolding for g10; pole/knot coordinates omitted)
    g10: BSplineCurve PolesCount=5 KnotsCount=3 Degree=3 IsPeriodic=0
    g11: GeomPoint [constr] X=12.1 Y=7.05 Z=0
    g12: GeomPoint [constr] X=11.1765 Y=5.88818 Z=0
    g13: GeomPoint [constr] X=7.9 Y=5 Z=0
  constraints (23):
    c: PointOnObject(g0,g-2)
    c: Horizontal(g0)
    c: Coincident(g0,g1)
    c: Coincident(g1,g-3)
    c: Coincident(g1,g2)
    c: Horizontal(g2)
    c: DistanceY(g0) = 5
    c: DistanceX(g0,g0) = 7.9
    c: DistanceX(g2,g2) = 20.05
    c: DistanceX(g3) = 12.1
    c: DistanceY(g0,g3) = 2.05
    c: Coincident(g4,g3)
    c: Tangent(g4,g2) = 1.5708
    c: Tangent(g3,g4,g3) = -1.5708
    c: Radius(g4) = 2.15
    c: Weight(g5) = 1
    c: Equal(g5, g6-g9) x4
    c: InternalAlignment(g5-g9 -> g10) x5
    c: InternalAlignment(g11,g10)
    c: InternalAlignment(g12,g10)
    c: InternalAlignment(g13,g10)
    c: Coincident(g5,g3)
    c: Coincident(g9,g0)
FEATURE [PartDesign::Pocket] Pocket008
  BaseFeature = -> Pad001
  Direction = (0,1,-2e-16)
  Length = 5
  Length2 = 5
  Profile = -> Sketch010
  ReferenceAxis = -> Sketch010 [N_Axis]
  Refine = true
  Suppressed = false
  Type = 1
FEATURE [Sketcher::SketchObject] Sketch011
  ArcFitTolerance = 1e-06
  AttachmentSupport = -> [Pocket008]
  ExternalGeometry = -> [Pocket008]
  FullyConstrained = true
  MakeInternals = false
  MapMode = 5
  Placement = pos=(0,0,21) rot=(0,0,1;0rad)
  sketch-geometry (13):
    g0: LineSegment StartX=11 StartY=30.8 StartZ=0 EndX=11 EndY=0 EndZ=0
    g1: LineSegment StartX=11 StartY=0 StartZ=0 EndX=23.3 EndY=0 EndZ=0
    g2: LineSegment StartX=23.3 StartY=0 StartZ=0 EndX=23.3 EndY=22.3 EndZ=0
    g3: LineSegment StartX=23.3 StartY=22.3 StartZ=0 EndX=59.9 EndY=22.3 EndZ=0
    g4: LineSegment StartX=59.9 StartY=22.3 StartZ=0 EndX=59.9 EndY=10.55 EndZ=0
    g5: LineSegment StartX=59.9 StartY=10.55 StartZ=0 EndX=72.15 EndY=10.55 EndZ=0
    g6: LineSegment StartX=72.15 StartY=10.55 StartZ=0 EndX=72.15 EndY=0 EndZ=0
    g7: LineSegment StartX=72.15 StartY=0 StartZ=0 EndX=73.35 EndY=0 EndZ=0
    g8: LineSegment StartX=73.35 StartY=27.75 StartZ=0 EndX=25.4 EndY=27.75 EndZ=0
    g9: LineSegment StartX=24.2 StartY=28.95 StartZ=0 EndX=24.2 EndY=30.8 EndZ=0
    g10: LineSegment StartX=24.2 StartY=30.8 StartZ=0 EndX=11 EndY=30.8 EndZ=0
    g11: ArcOfCircle CenterX=25.4 CenterY=28.95 CenterZ=0 NormalX=0 NormalY=0 NormalZ=1 AngleXU=0 Radius=1.2 StartAngle=3.14159 EndAngle=4.71239
    g12: LineSegment StartX=73.35 StartY=27.75 StartZ=0 EndX=73.35 EndY=0 EndZ=0
  constraints (33):
    c: Vertical(g0)
    c: Coincident(g0,g1)
    c: PointOnObject(g1,g-1)
    c: Coincident(g1,g2)
    c: Coincident(g2,g-4)
    c: Vertical(g2)
    c: Coincident(g2,g3)
    c: Coincident(g3,g-4)
    c: Coincident(g3,g4)
    c: Coincident(g4,g-3)
    c: Coincident(g4,g5)
    c: Coincident(g5,g-3)
    c: Coincident(g5,g6)
    c: PointOnObject(g6,g-1)
    c: Vertical(g6)
    c: Coincident(g6,g7)
    c: PointOnObject(g7,g-1)
    c: Horizontal(g8)
    c: Vertical(g9)
    c: Coincident(g9,g10)
    c: Coincident(g10,g0)
    c: Horizontal(g10)
    c: Tangent(g11,g8) = 1.5708
    c: Tangent(g11,g9) = 1.5708
    c: DistanceY(g0) = 30.8
    c: DistanceX(g9) = 24.2
    c: DistanceY(g8) = 27.75
    c: Radius(g11) = 1.2
    c: DistanceX(g8,g8) = 47.95
    c: Coincident(g12,g8)
    c: Coincident(g12,g7)
    c: Vertical(g12)
    c: Coincident(g0,g-5)
FEATURE [PartDesign::Pocket] Pocket009
  BaseFeature = -> Pocket008
  Direction = (0,0,-1)
  Length = 15
  Length2 = 5
  Profile = -> Sketch011
  ReferenceAxis = -> Sketch011 [N_Axis]
  Refine = true
  Suppressed = false
  Type = 0
FEATURE [Sketcher::SketchObject] Sketch012
  ArcFitTolerance = 1e-06
  AttachmentSupport = -> [Pocket009]
  ExternalGeometry = -> [Pocket009]
  FullyConstrained = true
  MakeInternals = false
  MapMode = 5
  Placement = pos=(0,0,0) rot=(1,0,0;1.5708rad)
  sketch-geometry (3):
    g0: LineSegment StartX=16.7 StartY=6 StartZ=0 EndX=11 EndY=6 EndZ=0
    g1: LineSegment StartX=11 StartY=6 StartZ=0 EndX=11 EndY=2 EndZ=0
    g2: LineSegment StartX=11 StartY=2 StartZ=0 EndX=16.7 EndY=6 EndZ=0
  constraints (9):
    c: PointOnObject(g0,g-3)
    c: Horizontal(g0)
    c: Coincident(g0,g1)
    c: PointOnObject(g1,g-4)
    c: Coincident(g1,g2)
    c: Coincident(g2,g0)
    c: Vertical(g1)
    c: DistanceX(g0,g0) = 5.7
    c: DistanceY(g1,g1) = 4
FEATURE [PartDesign::Pocket] Pocket010
  BaseFeature = -> Pocket009
  Direction = (0,1,-2e-16)
  Length = 0
  Length2 = 5
  Profile = -> Sketch012
  ReferenceAxis = -> Sketch012 [N_Axis]
  Refine = true
  Suppressed = false
  Type = 3
  UpToFace = -> Pocket009 [Face21]
FEATURE [Sketcher::SketchObject] Sketch013
  ArcFitTolerance = 1e-06
  AttachmentSupport = -> [Pocket010]
  ExternalGeometry = -> [Pocket010]
  FullyConstrained = true
  MakeInternals = false
  MapMode = 5
  Placement = pos=(0,0,0) rot=(1,0,0;3.14159rad)
  sketch-geometry (14):
    g0: LineSegment StartX=72.15 StartY=-10.55 StartZ=0 EndX=59.9 EndY=-10.55 EndZ=0
    g1: LineSegment StartX=59.9 StartY=-10.55 StartZ=0 EndX=59.9 EndY=-22.3 EndZ=0
    g2: LineSegment StartX=59.9 StartY=-22.3 StartZ=0 EndX=23.3 EndY=-22.3 EndZ=0
    g3: LineSegment StartX=23.3 StartY=-22.3 StartZ=0 EndX=23.3 EndY=-24.5 EndZ=0
    g4: LineSegment StartX=23.3 StartY=-24.5 StartZ=0 EndX=62.3 EndY=-24.5 EndZ=0
    g5: LineSegment StartX=62.3 StartY=-24.5 StartZ=0 EndX=62.3 EndY=-12.55 EndZ=0
    g6: LineSegment StartX=62.3 StartY=-12.55 StartZ=0 EndX=75.35 EndY=-12.55 EndZ=0
    g7: LineSegment StartX=75.35 StartY=-12.55 StartZ=0 EndX=75.35 EndY=0 EndZ=0
    g8: LineSegment StartX=75.35 StartY=0 StartZ=0 EndX=72.15 EndY=0 EndZ=0
    g9: LineSegment StartX=72.15 StartY=0 StartZ=0 EndX=72.15 EndY=-10.55 EndZ=0
    g10: LineSegment StartX=23.3 StartY=0 StartZ=0 EndX=21.3 EndY=0 EndZ=0
    g11: LineSegment StartX=21.3 StartY=0 StartZ=0 EndX=21.3 EndY=-12.5 EndZ=0
    g12: LineSegment StartX=21.3 StartY=-12.5 StartZ=0 EndX=23.3 EndY=-12.5 EndZ=0
    g13: LineSegment StartX=23.3 StartY=-12.5 StartZ=0 EndX=23.3 EndY=0 EndZ=0
  constraints (38):
    c: Coincident(g-3,g0)
    c: Coincident(g0,g-3)
    c: Coincident(g0,g1)
    c: Coincident(g1,g-4)
    c: Coincident(g1,g2)
    c: Coincident(g2,g-4)
    c: Coincident(g2,g3)
    c: Coincident(g3,g4)
    c: Horizontal(g4)
    c: Coincident(g4,g5)
    c: Vertical(g5)
    c: Coincident(g5,g6)
    c: Horizontal(g6)
    c: Coincident(g6,g7)
    c: PointOnObject(g7,g-1)
    c: Vertical(g7)
    c: Coincident(g7,g8)
    c: PointOnObject(g8,g-1)
    c: Coincident(g8,g9)
    c: Coincident(g9,g0)
    c: Vertical(g9)
    c: Vertical(g3)
    c: Coincident(g10,g11)
    c: Coincident(g11,g12)
    c: Coincident(g12,g13)
    c: Coincident(g13,g10)
    c: Horizontal(g10)
    c: Horizontal(g12)
    c: Vertical(g11)
    c: Vertical(g13)
    c: PointOnObject(g10,g-1)
    c: Vertical(g12,g2)
    c: DistanceY(g13,g13) = 12.5
    c: DistanceX(g10,g10) = 2
    c: DistanceY(g3,g3) = 2.2
    c: DistanceX(g0,g5) = 2.4
    c: DistanceX(g8,g8) = 3.2
    c: DistanceY(g5,g0) = 2
FEATURE [PartDesign::Pocket] Pocket011
  BaseFeature = -> Pocket010
  Direction = (0,0,1)
  Length = 4
  Length2 = 5
  Profile = -> Sketch013
  ReferenceAxis = -> Sketch013 [N_Axis]
  Refine = true
  Suppressed = false
  Type = 0
FEATURE [Sketcher::SketchObject] Sketch014
  ArcFitTolerance = 1e-06
  AttachmentSupport = -> [Pocket011]
  ExternalGeometry = -> [Pocket011]
  FullyConstrained = false
  MakeInternals = false
  MapMode = 5
  Placement = pos=(0,0,21) rot=(0,0,1;0rad)
  sketch-geometry (9):
    g0: LineSegment StartX=73.35 StartY=27.75 StartZ=0 EndX=73.35 EndY=0 EndZ=0
    g1: LineSegment StartX=73.35 StartY=0 StartZ=0 EndX=89.95 EndY=0 EndZ=0
    g2-g5: Circle [constr] x4 (B-spline internal-alignment scaffolding for g6; pole/knot coordinates omitted)
    g6: BSplineCurve PolesCount=4 KnotsCount=2 Degree=3 IsPeriodic=0
    g7: GeomPoint [constr] X=89.95 Y=0 Z=0
    g8: GeomPoint [constr] X=73.35 Y=27.75 Z=0
  constraints (14):
    c: Coincident(g-3,g0)
    c: Coincident(g0,g-3)
    c: Coincident(g0,g1)
    c: PointOnObject(g1,g-1)
    c: DistanceX(g1,g1) = 16.6
    c: Weight(g2) = 1
    c: Equal(g2,g3)
    c: Equal(g2,g4)
    c: Equal(g2,g5)
    c: InternalAlignment(g2-g5 -> g6) x4
    c: InternalAlignment(g7,g6)
    c: InternalAlignment(g8,g6)
    c: Coincident(g2,g1)
    c: Coincident(g5,g0)
FEATURE [PartDesign::Pocket] Pocket012
  BaseFeature = -> Pocket011
  Direction = (0,0,-1)
  Length = 3
  Length2 = 5
  Profile = -> Sketch014
  ReferenceAxis = -> Sketch014 [N_Axis]
  Refine = true
  Suppressed = false
  Type = 0
FEATURE [Sketcher::SketchObject] Sketch015
  ArcFitTolerance = 1e-06
  AttachmentSupport = -> [Pocket012]
  ExternalGeometry = -> [Pocket012]
  FullyConstrained = true
  MakeInternals = false
  MapMode = 5
  Placement = pos=(0,27.75,0) rot=(1,0,0;1.5708rad)
  sketch-geometry (7):
    g0: LineSegment StartX=24.2 StartY=6 StartZ=0 EndX=73.35 EndY=6 EndZ=0
    g1: LineSegment StartX=73.35 StartY=6 StartZ=0 EndX=73.35 EndY=15 EndZ=0
    g2: LineSegment StartX=73.35 StartY=15 StartZ=0 EndX=51 EndY=15 EndZ=0
    g3: LineSegment StartX=51 StartY=15 StartZ=0 EndX=48.45 EndY=16 EndZ=0
    g4: LineSegment StartX=48.45 StartY=16 StartZ=0 EndX=25 EndY=16 EndZ=0
    g5: LineSegment StartX=25 StartY=16 StartZ=0 EndX=24.2 EndY=16.4 EndZ=0
    g6: LineSegment StartX=24.2 StartY=16.4 StartZ=0 EndX=24.2 EndY=6 EndZ=0
  constraints (19):
    c: Coincident(g-3,g0)
    c: Coincident(g0,g-4)
    c: Coincident(g0,g1)
    c: PointOnObject(g1,g-4)
    c: Coincident(g1,g2)
    c: Horizontal(g2)
    c: Coincident(g2,g3)
    c: Coincident(g3,g4)
    c: Horizontal(g4)
    c: Coincident(g4,g5)
    c: PointOnObject(g5,g-3)
    c: Coincident(g5,g6)
    c: Coincident(g6,g0)
    c: DistanceY(g6,g6) = 10.4
    c: DistanceY(g4) = 16
    c: DistanceX(g5,g4) = 0.8
    c: DistanceX(g4,g4) = 23.45
    c: DistanceY(g2) = 15
    c: DistanceX(g2,g2) = 22.35
FEATURE [PartDesign::Pocket] Pocket013
  BaseFeature = -> Pocket012
  Direction = (0,1,-2e-16)
  Length = 0
  Length2 = 5
  Profile = -> Sketch015
  ReferenceAxis = -> Sketch015 [N_Axis]
  Refine = true
  Suppressed = false
  Type = 3
  UpToFace = -> Pocket012 [Face35]
FEATURE [Sketcher::SketchObject] Sketch016
  ArcFitTolerance = 1e-06
  AttachmentSupport = -> [XY_Plane002]
  FullyConstrained = false
  MakeInternals = false
  MapMode = 5
  sketch-geometry (36):
    g0: LineSegment [constr] StartX=23.3 StartY=22.3 StartZ=0 EndX=59.9 EndY=22.3 EndZ=0
    g1: LineSegment [constr] StartX=59.9 StartY=22.3 StartZ=0 EndX=59.9 EndY=10.55 EndZ=0
    g2: LineSegment [constr] StartX=59.9 StartY=10.55 StartZ=0 EndX=72.15 EndY=10.55 EndZ=0
    g3: LineSegment [constr] StartX=72.15 StartY=10.55 StartZ=0 EndX=72.15 EndY=0 EndZ=0
    g4: LineSegment [constr] StartX=72.15 StartY=0 StartZ=0 EndX=80.25 EndY=2e-16 EndZ=0
    g5: LineSegment [constr] StartX=83.75 StartY=0 StartZ=0 EndX=92 EndY=0 EndZ=0
    g6: ArcOfCircle [constr] CenterX=82 CenterY=0 CenterZ=0 NormalX=0 NormalY=0 NormalZ=1 AngleXU=0 Radius=1.75 StartAngle=0 EndAngle=3.14159
    g7: LineSegment [constr] StartX=0 StartY=6.35e-14 StartZ=0 EndX=5.5 EndY=0 EndZ=0
    g8: LineSegment [constr] StartX=5.5 StartY=0 StartZ=0 EndX=5.5 EndY=18 EndZ=0
    g9: LineSegment [constr] StartX=5.5 StartY=18 StartZ=0 EndX=11 EndY=18 EndZ=0
    g10: LineSegment [constr] StartX=11 StartY=0 StartZ=0 EndX=23.3 EndY=0 EndZ=0
    g11: LineSegment StartX=0.05 StartY=7.2 StartZ=0 EndX=0.75 EndY=22.55 EndZ=0
    g12: ArcOfCircle CenterX=518.425 CenterY=0 CenterZ=0 NormalX=0 NormalY=0 NormalZ=1 AngleXU=0 Radius=518.425 StartAngle=3.1277 EndAngle=3.14159
    g13: LineSegment [constr] StartX=11 StartY=0 StartZ=0 EndX=11 EndY=18 EndZ=0
    g14: LineSegment StartX=20.1 StartY=35.5 StartZ=0 EndX=64.2 EndY=35.5 EndZ=0
    g15-g20: Circle [constr] x6 (B-spline internal-alignment scaffolding for g21; pole/knot coordinates omitted)
    g21: BSplineCurve PolesCount=6 KnotsCount=4 Degree=3 IsPeriodic=0
    g22-g25: GeomPoint [constr] x4 (B-spline internal-alignment scaffolding for g21; pole/knot coordinates omitted)
    g26-g29: Circle [constr] x4 (B-spline internal-alignment scaffolding for g30; pole/knot coordinates omitted)
    g30: BSplineCurve PolesCount=4 KnotsCount=2 Degree=3 IsPeriodic=0
    g31: GeomPoint [constr] X=92 Y=0 Z=0
    g32: GeomPoint [constr] X=64.2 Y=35.5 Z=0
    g33: Circle [constr] CenterX=17 CenterY=25 CenterZ=0 NormalX=0 NormalY=0 NormalZ=1 AngleXU=0 Radius=1.75
    g34: LineSegment [constr] StartX=23.3 StartY=0 StartZ=0 EndX=23.3 EndY=22.3 EndZ=0
    g35: LineSegment StartX=0 StartY=6.35e-14 StartZ=0 EndX=92 EndY=0 EndZ=0
  constraints (73):
    c: PointOnObject(g10,g-1)
    c: Horizontal(g0)
    c: Coincident(g0,g1)
    c: Vertical(g1)
    c: Coincident(g1,g2)
    c: Horizontal(g2)
    c: Coincident(g2,g3)
    c: PointOnObject(g3,g-1)
    c: Vertical(g3)
    c: Coincident(g4,g3)
    c: PointOnObject(g4,g-1)
    c: PointOnObject(g5,g-1)
    c: PointOnObject(g5,g-1)
    c: Coincident(g6,g4)
    c: Coincident(g6,g5)
    c: PointOnObject(g6,g-1)
    c: Coincident(g7,g-1)
    c: PointOnObject(g7,g-1)
    c: Coincident(g8,g7)
    c: Vertical(g8)
    c: Horizontal(g9)
    c: PointOnObject(g10,g-1)
    c: DistanceX(g7,g7) = 5.5
    c: DistanceX(g7,g10) = 5.5
    c: Coincident(g9,g8)
    c: DistanceY(g8,g8) = 18
    c: Diameter(g6) = 3.5
    c: DistanceX(g5,g5) = 8.25
    c: DistanceX(g5) = 92
    c: DistanceX(g11) = 0.75
    c: DistanceY(g11) = 22.55
    c: Coincident(g12,g7)
    c: Coincident(g12,g11)
    c: DistanceX(g11) = 0.05
    c: DistanceY(g11) = 7.2
    c: Perpendicular(g12,g-1)
    c: Radius(g12) = 518.425
    c: Coincident(g13,g10)
    c: Coincident(g13,g9)
    c: Vertical(g13)
    c: Horizontal(g14)
    c: DistanceY(g14) = 35.5
    c: DistanceX(g14) = 20.1
    c: DistanceX(g14,g14) = 44.1
    c: Weight(g15) = 1
    c: Equal(g15, g16-g20) x5
    c: InternalAlignment(g15-g20 -> g21) x6
    c: InternalAlignment(g22-g25 -> g21) x4
    c: Coincident(g15,g11)
    c: Coincident(g20,g14)
    c: Weight(g26) = 1
    c: Equal(g26,g27)
    c: Equal(g26,g28)
    c: Equal(g26,g29)
    c: InternalAlignment(g26-g29 -> g30) x4
    c: InternalAlignment(g31,g30)
    c: InternalAlignment(g32,g30)
    c: Coincident(g26,g5)
    c: Coincident(g29,g14)
    c: DistanceY(g33) = 25
    c: DistanceX(g33,g6) = 65
    c: Equal(g33,g6)
    c: Coincident(g34,g10)
    c: Coincident(g34,g0)
    c: Vertical(g34)
    c: DistanceX(g10,g10) = 12.3
    c: DistanceY(g34,g34) = 22.3
    c: DistanceX(g0,g0) = 36.6
    c: DistanceY(g1,g1) = 11.75
    c: DistanceX(g2,g2) = 12.25
    c: DistanceX(g4,g4) = 8.1
    c: Coincident(g35,g7)
    c: Coincident(g35,g30)
FEATURE [PartDesign::Pad] Pad002
  Direction = (0,0,1)
  Length = 12
  Length2 = 10
  Profile = -> Sketch016
  ReferenceAxis = -> Sketch016 [N_Axis]
  Refine = true
  Suppressed = false
  Type = 0
FEATURE [Sketcher::SketchObject] Sketch017
  ArcFitTolerance = 1e-06
  AttachmentSupport = -> [Pad002]
  ExternalGeometry = -> [Pad002]
  FullyConstrained = true
  MakeInternals = false
  MapMode = 5
  Placement = pos=(0,0,12) rot=(0,0,1;0rad)
  sketch-geometry (36):
    g0: ArcOfCircle CenterX=82 CenterY=0 CenterZ=0 NormalX=0 NormalY=0 NormalZ=1 AngleXU=0 Radius=2.5 StartAngle=0 EndAngle=3.14159
    g1: Circle CenterX=17 CenterY=25 CenterZ=0 NormalX=0 NormalY=0 NormalZ=1 AngleXU=0 Radius=2.5
    g2: LineSegment StartX=2 StartY=0 StartZ=0 EndX=2.57586 EndY=18.6857 EndZ=0
    g3: ArcOfCircle CenterX=82 CenterY=0 CenterZ=0 NormalX=0 NormalY=0 NormalZ=1 AngleXU=0 Radius=6 StartAngle=1.5708 EndAngle=3.14159
    g4: ArcOfCircle CenterX=85.5 CenterY=8 CenterZ=0 NormalX=0 NormalY=0 NormalZ=1 AngleXU=0 Radius=2 StartAngle=4.71239 EndAngle=6.19002
    g5: ArcOfCircle CenterX=17 CenterY=25 CenterZ=0 NormalX=0 NormalY=0 NormalZ=1 AngleXU=0 Radius=6 StartAngle=3.14159 EndAngle=6.28319
    g6: ArcOfCircle CenterX=25 CenterY=31.5 CenterZ=0 NormalX=0 NormalY=0 NormalZ=1 AngleXU=0 Radius=2 StartAngle=1.5708 EndAngle=3.14159
    g7: ArcOfCircle CenterX=9 CenterY=28 CenterZ=0 NormalX=0 NormalY=0 NormalZ=1 AngleXU=0 Radius=2 StartAngle=2e-16 EndAngle=2.29046
    g8: ArcOfCircle CenterX=17.5687 CenterY=18.2237 CenterZ=0 NormalX=0 NormalY=0 NormalZ=1 AngleXU=0 Radius=15 StartAngle=2.29046 EndAngle=3.11078
    g9: LineSegment StartX=23 StartY=25 StartZ=0 EndX=23 EndY=31.5 EndZ=0
    g10: LineSegment StartX=11 StartY=25 StartZ=0 EndX=11 EndY=28 EndZ=0
    g11: LineSegment StartX=82 StartY=6 StartZ=0 EndX=85.5 EndY=6 EndZ=0
    g12: ArcOfCircle CenterX=64.0932 CenterY=10.0002 CenterZ=0 NormalX=0 NormalY=0 NormalZ=1 AngleXU=0 Radius=23.5 StartAngle=6.19002 EndAngle=7.84944
    g13: LineSegment StartX=79.5 StartY=0 StartZ=0 EndX=84.5 EndY=0 EndZ=0
    g14: LineSegment StartX=2 StartY=0 StartZ=0 EndX=16 EndY=0 EndZ=0
    g15: LineSegment StartX=16 StartY=0 StartZ=0 EndX=16 EndY=1 EndZ=0
    g16: LineSegment StartX=16 StartY=1 StartZ=0 EndX=22 EndY=1 EndZ=0
    g17: LineSegment StartX=22 StartY=1 StartZ=0 EndX=22 EndY=8e-16 EndZ=0
    g18: LineSegment StartX=22 StartY=8e-16 StartZ=0 EndX=76 EndY=8e-16 EndZ=0
    g19: ArcOfCircle CenterX=28 CenterY=31.5 CenterZ=0 NormalX=0 NormalY=0 NormalZ=1 AngleXU=0 Radius=2 StartAngle=2e-16 EndAngle=1.5708
    g20: ArcOfCircle CenterX=32 CenterY=12 CenterZ=0 NormalX=0 NormalY=0 NormalZ=1 AngleXU=0 Radius=2 StartAngle=3.14159 EndAngle=4.71239
    g21: ArcOfCircle CenterX=34 CenterY=12 CenterZ=0 NormalX=0 NormalY=0 NormalZ=1 AngleXU=0 Radius=2 StartAngle=4.71239 EndAngle=6.28319
    g22: ArcOfCircle CenterX=38 CenterY=31.5 CenterZ=0 NormalX=0 NormalY=0 NormalZ=1 AngleXU=0 Radius=2 StartAngle=1.5708 EndAngle=3.14159
    g23: ArcOfCircle CenterX=45.2 CenterY=31.5 CenterZ=0 NormalX=0 NormalY=0 NormalZ=1 AngleXU=0 Radius=2 StartAngle=4e-16 EndAngle=1.5708
    g24: ArcOfCircle CenterX=49.2 CenterY=12 CenterZ=0 NormalX=0 NormalY=0 NormalZ=1 AngleXU=0 Radius=2 StartAngle=3.14159 EndAngle=4.71239
    g25: ArcOfCircle CenterX=51.2 CenterY=12 CenterZ=0 NormalX=0 NormalY=0 NormalZ=1 AngleXU=0 Radius=2 StartAngle=4.71239 EndAngle=6.28319
    g26: ArcOfCircle CenterX=55.2 CenterY=31.5 CenterZ=0 NormalX=0 NormalY=0 NormalZ=1 AngleXU=0 Radius=2 StartAngle=1.5708 EndAngle=3.14159
    g27: LineSegment StartX=55.2 StartY=33.5 StartZ=0 EndX=64.2 EndY=33.5 EndZ=0
    g28: LineSegment StartX=53.2 StartY=31.5 StartZ=0 EndX=53.2 EndY=12 EndZ=0
    g29: LineSegment StartX=51.2 StartY=10 StartZ=0 EndX=49.2 EndY=10 EndZ=0
    g30: LineSegment StartX=47.2 StartY=12 StartZ=0 EndX=47.2 EndY=31.5 EndZ=0
    g31: LineSegment StartX=45.2 StartY=33.5 StartZ=0 EndX=38 EndY=33.5 EndZ=0
    g32: LineSegment StartX=36 StartY=31.5 StartZ=0 EndX=36 EndY=12 EndZ=0
    g33: LineSegment StartX=34 StartY=10 StartZ=0 EndX=32 EndY=10 EndZ=0
    g34: LineSegment StartX=30 StartY=12 StartZ=0 EndX=30 EndY=31.5 EndZ=0
    g35: LineSegment StartX=28 StartY=33.5 StartZ=0 EndX=25 EndY=33.5 EndZ=0
  constraints (96):
    c: PointOnObject(g0,g-1)
    c: PointOnObject(g0,g-1)
    c: PointOnObject(g0,g-1)
    c: PointOnObject(g2,g-1)
    c: DistanceX(g-1,g2) = 2
    c: Vertical(g12,g-3)
    c: DistanceY(g12,g-3) = 2
    c: Vertical(g10)
    c: Tangent(g11,g4) = -1.5708
    c: Tangent(g11,g3) = 1.5708
    c: Tangent(g9,g6) = 1.5708
    c: Tangent(g9,g5) = -1.5708
    c: Tangent(g10,g5) = 1.5708
    c: Tangent(g10,g7) = -1.5708
    c: Vertical(g9)
    c: Coincident(g5,g1)
    c: Coincident(g3,g0)
    c: Horizontal(g11)
    c: Tangent(g8,g7) = -1.5708
    c: Equal(g1,g0)
    c: Diameter(g0) = 5
    c: Tangent(g12,g4) = -1.5708
    c: Radius(g3) = 6
    c: Equal(g7,g6)
    c: Equal(g4,g6)
    c: Radius(g4) = 2
    c: Tangent(g8,g2) = 1.5708
    c: Equal(g3,g5)
    c: DistanceY(g1) = 25
    c: DistanceX(g1) = 17
    c: DistanceX(g1,g0) = 65
    c: Radius(g12) = 23.5
    c: Distance(g2,g-4) = 2
    c: Radius(g8) = 15
    c: DistanceY(g10,g10) = 3
    c: Coincident(g13,g0)
    c: Coincident(g13,g0)
    c: Coincident(g2,g14)
    c: PointOnObject(g14,g-1)
    c: Coincident(g14,g15)
    c: Coincident(g15,g16)
    c: Coincident(g16,g17)
    c: PointOnObject(g17,g-1)
    c: Vertical(g17)
    c: Coincident(g17,g18)
    c: Coincident(g18,g3)
    c: Horizontal(g18)
    c: DistanceX(g14) = 16
    c: Horizontal(g16)
    c: DistanceY(g15) = 1
    c: DistanceX(g16,g16) = 6
    c: Vertical(g15)
    c: Coincident(g27,g12)
    c: Horizontal(g31)
    c: Vertical(g32)
    c: Horizontal(g35)
    c: Tangent(g35,g6) = -1.5708
    c: Tangent(g35,g19) = -1.5708
    c: Tangent(g34,g19) = -1.5708
    c: Tangent(g34,g20) = 1.5708
    c: Tangent(g33,g20) = 1.5708
    c: Tangent(g33,g21) = 1.5708
    c: Tangent(g32,g21) = 1.5708
    c: Tangent(g32,g22) = -1.5708
    c: Tangent(g31,g22) = -1.5708
    c: Tangent(g31,g23) = -1.5708
    c: Tangent(g30,g23) = -1.5708
    c: Tangent(g30,g24) = 1.5708
    c: Tangent(g29,g24) = 1.5708
    c: Tangent(g29,g25) = 1.5708
    c: Tangent(g28,g25) = 1.5708
    c: Tangent(g27,g26) = 1.5708
    c: Tangent(g28,g26) = -1.5708
    c: Horizontal(g27)
    c: Vertical(g34)
    c: Horizontal(g33)
    c: Vertical(g30)
    c: Vertical(g28)
    c: Horizontal(g29)
    c: Horizontal(g23,g26)
    c: Horizontal(g24,g21)
    c: Equal(g25,g24)
    c: Equal(g24,g21)
    c: Equal(g21,g20)
    c: Horizontal(g19,g22)
    c: Equal(g19,g22)
    c: Equal(g22,g23)
    c: Equal(g23,g26)
    c: Equal(g6,g19)
    c: Equal(g19,g20)
    c: Equal(g33,g29)
    c: DistanceX(g35,g35) = 3
    c: DistanceX(g27,g27) = 9
    c: DistanceX(g33,g33) = 2
    c: DistanceY(g21) = 10
    c: DistanceX(g11,g11) = 3.5
FEATURE [TechDraw::DrawSVGTemplate] Template001
  EditableTexts = approval_person=B. Hecate; creator=Jon Sagebrand; date_of_issue=2026-02-18; document_type=Component Drawing; general_tolerances=ISO 2768-m; identification_number=DN; language_code=EN; legal_owner_1=Jonix; part_material=PETG; revision_index=AAA; scale=1 : 1; sheet_number=2 / 2; title=Makita LXT  - 18V - Battery holder
  Height = 210
  Orientation = 1
  Template = <path>
  Width = 297
FEATURE [TechDraw::DrawProjGroupItem] View001  label="Front"
  CoarseView = false
  Direction = (0,0,1)
  Focus = 100
  HardHidden = false
  IsoCount = 0
  IsoHidden = false
  IsoVisible = false
  LockPosition = true
  Perspective = false
  Rotation = 0
  RotationVector = (1,0,0)
  ScaleType = 2
  ScrubCount = 1
  SeamHidden = false
  SeamVisible = false
  SmoothHidden = false
  SmoothVisible = true
  Source = -> [Pocket013]
  Type = 0
  X = 0
  XDirection = (1,0,0)
  Y = 0
FEATURE [TechDraw::DrawProjGroupItem] ProjItem  label="Bottom"
  CoarseView = false
  Direction = (0,-1,0)
  Focus = 100
  HardHidden = false
  IsoCount = 0
  IsoHidden = false
  IsoVisible = false
  LockPosition = false
  Perspective = false
  Rotation = 0
  RotationVector = (1,0,0)
  ScaleType = 0
  ScrubCount = 1
  SeamHidden = false
  SeamVisible = false
  SmoothHidden = false
  SmoothVisible = true
  Source = -> [Pocket013]
  Type = 5
  X = 0
  XDirection = (1,0,0)
  Y = 43.25
FEATURE [TechDraw::DrawProjGroup] ProjGroup
  Anchor = -> View001
  AutoDistribute = true
  LockPosition = false
  ProjectionType = 0
  Rotation = 0
  ScaleType = 0
  Source = -> [Pocket013]
  Views = -> [View001,ProjItem]
  X = 148.5
  Y = 105
  spacingX = 15
  spacingY = 15
FEATURE [TechDraw::DrawViewDimension] Dimension006
  AngleOverride = false
  Arbitrary = false
  ArbitraryTolerances = false
  BoxCorners = (2) [(-46.0118,-17.75,-1e-07),(46.0118,17.75,1e-07)]
  EqualTolerance = true
  ExtensionAngle = 0
  FormatSpec = %.2w
  FormatSpecOverTolerance = %+.2w
  FormatSpecUnderTolerance = %+.2w
  Inverted = false
  LineAngle = 0
  LockPosition = false
  MeasureType = 1
  OverTolerance = 0
  References2D = -> [View001]
  Rotation = 0
  ScaleType = 0
  TheoreticalExact = false
  Type = 2
  UnderTolerance = 0
  X = -58.8145
  Y = -5.25
FEATURE [TechDraw::DrawViewDimension] Dimension007
  AngleOverride = false
  Arbitrary = false
  ArbitraryTolerances = false
  BoxCorners = (2) [(-46.0118,-17.75,-1e-07),(46.0118,17.75,1e-07)]
  EqualTolerance = true
  ExtensionAngle = 0
  FormatSpec = %.2w
  FormatSpecOverTolerance = %+.2w
  FormatSpecUnderTolerance = %+.2w
  Inverted = false
  LineAngle = 0
  LockPosition = false
  MeasureType = 1
  OverTolerance = 0
  References2D = -> [View001]
  Rotation = 0
  ScaleType = 0
  TheoreticalExact = false
  Type = 1
  UnderTolerance = 0
  X = -37.5118
  Y = -29.5131
FEATURE [TechDraw::DrawViewDimension] Dimension008
  AngleOverride = false
  Arbitrary = false
  ArbitraryTolerances = false
  BoxCorners = (2) [(-46.0118,-17.75,-1e-07),(46.0118,17.75,1e-07)]
  EqualTolerance = true
  ExtensionAngle = 0
  FormatSpec = %.2w
  FormatSpecOverTolerance = %+.2w
  FormatSpecUnderTolerance = %+.2w
  Inverted = false
  LineAngle = 0
  LockPosition = false
  MeasureType = 1
  OverTolerance = 0
  References2D = -> [View001]
  Rotation = 0
  ScaleType = 0
  TheoreticalExact = false
  Type = 1
  UnderTolerance = 0
  X = 3.48819
  Y = -29.5131
FEATURE [TechDraw::DrawPage] Page001
  KeepUpdated = true
  NextBalloonIndex = 1
  ProjectionType = 0
  Template = -> Template001
  Views = -> [ProjGroup,Dimension006,Dimension007,Dimension008]
FEATURE [PartDesign::Pocket] Pocket014
  BaseFeature = -> Pad002
  Direction = (0,0,-1)
  Length = 0
  Length2 = 5
  Offset = -2
  Profile = -> Sketch017
  ReferenceAxis = -> Sketch017 [N_Axis]
  Refine = true
  Suppressed = false
  Type = 3
  UpToFace = -> Pad002 [Face7]
FEATURE [Sketcher::SketchObject] Sketch018
  ArcFitTolerance = 1e-06
  AttachmentSupport = -> [Pocket014]
  ExternalGeometry = -> [Pocket014]
  FullyConstrained = true
  MakeInternals = false
  MapMode = 5
  Placement = pos=(0,6.35e-14,0) rot=(1,0,0;1.5708rad)
  sketch-geometry (5):
    g0: LineSegment StartX=22 StartY=12 StartZ=0 EndX=22 EndY=4 EndZ=0
    g1: LineSegment StartX=22 StartY=4 StartZ=0 EndX=18 EndY=10 EndZ=0
    g2: LineSegment StartX=18 StartY=10 StartZ=0 EndX=16 EndY=10 EndZ=0
    g3: LineSegment StartX=16 StartY=10 StartZ=0 EndX=16 EndY=12 EndZ=0
    g4: LineSegment StartX=16 StartY=12 StartZ=0 EndX=22 EndY=12 EndZ=0
  constraints (13):
    c: Vertical(g0)
    c: Coincident(g0,g1)
    c: Coincident(g1,g2)
    c: Horizontal(g2)
    c: Coincident(g2,g3)
    c: Coincident(g3,g-3)
    c: Vertical(g3)
    c: Coincident(g3,g4)
    c: Coincident(g4,g-3)
    c: Coincident(g0,g4)
    c: DistanceY(g-4,g0) = 2
    c: DistanceY(g-4,g1) = 8
    c: DistanceX(g2,g2) = 2
FEATURE [PartDesign::Pocket] Pocket015
  BaseFeature = -> Pocket014
  Direction = (0,1,-2e-16)
  Length = 5
  Length2 = 5
  Profile = -> Sketch018
  ReferenceAxis = -> Sketch018 [N_Axis]
  Refine = true
  Suppressed = false
  Type = 2
FEATURE [Sketcher::SketchObject] Sketch019
  ArcFitTolerance = 1e-06
  AttachmentSupport = -> [YZ_Plane002]
  FullyConstrained = true
  MakeInternals = false
  MapMode = 5
  Placement = pos=(0,0,0) rot=(0.57735,0.57735,0.57735;2.0944rad)
  sketch-geometry (4):
    g0: LineSegment StartX=0 StartY=2 StartZ=0 EndX=8 EndY=2 EndZ=0
    g1: LineSegment StartX=8 StartY=2 StartZ=0 EndX=8 EndY=10.3 EndZ=0
    g2: LineSegment StartX=8 StartY=10.3 StartZ=0 EndX=0 EndY=10.3 EndZ=0
    g3: LineSegment StartX=0 StartY=10.3 StartZ=0 EndX=0 EndY=2 EndZ=0
  constraints (12):
    c: Coincident(g0,g1)
    c: Coincident(g1,g2)
    c: Coincident(g2,g3)
    c: Coincident(g3,g0)
    c: Horizontal(g0)
    c: Horizontal(g2)
    c: Vertical(g1)
    c: Vertical(g3)
    c: PointOnObject(g0,g-2)
    c: DistanceX(g2,g2) = 8
    c: DistanceY(g3,g3) = 8.3
    c: DistanceY(g0) = 2
FEATURE [PartDesign::Pocket] Pocket016
  BaseFeature = -> Pocket015
  Direction = (-1,0,0)
  Length = 5
  Length2 = 5
  Profile = -> Sketch019
  ReferenceAxis = -> Sketch019 [N_Axis]
  Refine = true
  Reversed = true
  Suppressed = false
  Type = 0
FEATURE [Sketcher::SketchObject] Sketch020
  ArcFitTolerance = 1e-06
  AttachmentSupport = -> [Pocket013]
  ExternalGeometry = -> [Pocket013]
  FullyConstrained = true
  MakeInternals = false
  MapMode = 5
  Placement = pos=(0,0,18) rot=(0,0,1;0rad)
  sketch-geometry (2):
    g0: ArcOfCircle CenterX=82 CenterY=0 CenterZ=0 NormalX=0 NormalY=0 NormalZ=1 AngleXU=0 Radius=3 StartAngle=0 EndAngle=3.14159
    g1: LineSegment StartX=79 StartY=4e-16 StartZ=0 EndX=85 EndY=0 EndZ=0
  constraints (6):
    c: Coincident(g0,g-3)
    c: PointOnObject(g0,g-1)
    c: PointOnObject(g0,g-1)
    c: Diameter(g0) = 6
    c: Coincident(g1,g0)
    c: Coincident(g1,g0)
FEATURE [PartDesign::Pocket] Pocket017
  BaseFeature = -> Pocket013
  Direction = (0,0,-1)
  Length = 3
  Length2 = 5
  Profile = -> Sketch020
  ReferenceAxis = -> Sketch020 [N_Axis]
  Refine = true
  Suppressed = false
  Type = 0
FEATURE [Sketcher::SketchObject] Sketch021
  ArcFitTolerance = 1e-06
  AttachmentSupport = -> [Pocket017]
  ExternalGeometry = -> [Pocket017]
  FullyConstrained = true
  MakeInternals = false
  MapMode = 5
  Placement = pos=(0,0,6) rot=(0,0,1;0rad)
  sketch-geometry (1):
    g0: Circle CenterX=17 CenterY=25 CenterZ=0 NormalX=0 NormalY=0 NormalZ=1 AngleXU=0 Radius=3
  constraints (2):
    c: Coincident(g0,g-3)
    c: Diameter(g0) = 6
FEATURE [PartDesign::Pocket] Pocket018
  BaseFeature = -> Pocket017
  Direction = (0,0,-1)
  Length = 3
  Length2 = 5
  Profile = -> Sketch021
  ReferenceAxis = -> Sketch021 [N_Axis]
  Refine = true
  Suppressed = false
  Type = 0
FEATURE [PartDesign::Mirrored] Mirrored
  BaseFeature = -> Pocket018
  MirrorPlane = -> XZ_Plane001
  Originals = -> [Pocket018]
  Refine = true
  Suppressed = false
  TransformMode = 1
FEATURE [PartDesign::Body] Body001  label="Battery Mount v2"
  AllowCompound = false
  Group = -> [Sketch009,Pad001,Sketch010,Pocket008,Sketch011,Pocket009,Sketch012,Pocket010,Sketch013,Pocket011,Sketch014,Pocket012,Sketch015,Pocket013,Sketch020,Pocket017,Sketch021,Pocket018,Mirrored]
  Origin = -> Origin001
  Tip = -> Mirrored
FEATURE [Sketcher::SketchObject] Sketch022
  ArcFitTolerance = 1e-06
  AttachmentSupport = -> [Pocket016]
  ExternalGeometry = -> [Pocket016]
  FullyConstrained = true
  MakeInternals = false
  MapMode = 5
  Placement = pos=(0,0,12) rot=(0,0,1;0rad)
  sketch-geometry (16):
    g0: ArcOfCircle CenterX=34 CenterY=12 CenterZ=0 NormalX=0 NormalY=0 NormalZ=1 AngleXU=0 Radius=2 StartAngle=4.71239 EndAngle=6.28319
    g1: ArcOfCircle CenterX=32 CenterY=12 CenterZ=0 NormalX=0 NormalY=0 NormalZ=1 AngleXU=0 Radius=2 StartAngle=3.14159 EndAngle=4.71239
    g2: ArcOfCircle CenterX=49.2 CenterY=12 CenterZ=0 NormalX=0 NormalY=0 NormalZ=1 AngleXU=0 Radius=2 StartAngle=3.14159 EndAngle=4.71239
    g3: ArcOfCircle CenterX=51.2 CenterY=12 CenterZ=0 NormalX=0 NormalY=0 NormalZ=1 AngleXU=0 Radius=2 StartAngle=4.71239 EndAngle=6.28319
    g4: LineSegment StartX=32 StartY=10 StartZ=0 EndX=34 EndY=10 EndZ=0
    g5: LineSegment StartX=49.2 StartY=10 StartZ=0 EndX=51.2 EndY=10 EndZ=0
    g6: ArcOfCircle CenterX=32 CenterY=14 CenterZ=0 NormalX=0 NormalY=0 NormalZ=1 AngleXU=0 Radius=2 StartAngle=1.5708 EndAngle=3.14159
    g7: ArcOfCircle CenterX=34 CenterY=14 CenterZ=0 NormalX=0 NormalY=0 NormalZ=1 AngleXU=0 Radius=2 StartAngle=0 EndAngle=1.5708
    g8: ArcOfCircle CenterX=49.2 CenterY=14 CenterZ=0 NormalX=0 NormalY=0 NormalZ=1 AngleXU=0 Radius=2 StartAngle=1.5708 EndAngle=3.14159
    g9: ArcOfCircle CenterX=51.2 CenterY=14 CenterZ=0 NormalX=0 NormalY=0 NormalZ=1 AngleXU=0 Radius=2 StartAngle=2e-16 EndAngle=1.5708
    g10: LineSegment StartX=53.2 StartY=12 StartZ=0 EndX=53.2 EndY=14 EndZ=0
    g11: LineSegment StartX=47.2 StartY=12 StartZ=0 EndX=47.2 EndY=14 EndZ=0
    g12: LineSegment StartX=49.2 StartY=16 StartZ=0 EndX=51.2 EndY=16 EndZ=0
    g13: LineSegment StartX=36 StartY=12 StartZ=0 EndX=36 EndY=14 EndZ=0
    g14: LineSegment StartX=30 StartY=12 StartZ=0 EndX=30 EndY=14 EndZ=0
    g15: LineSegment StartX=32 StartY=16 StartZ=0 EndX=34 EndY=16 EndZ=0
  constraints (44):
    c: Coincident(g0,g-5)
    c: Coincident(g0,g-5)
    c: Coincident(g1,g-6)
    c: Coincident(g1,g-6)
    c: Coincident(g2,g-3)
    c: Coincident(g2,g-3)
    c: Coincident(g3,g-4)
    c: Coincident(g3,g-4)
    c: Coincident(g4,g1)
    c: Coincident(g4,g0)
    c: Coincident(g5,g2)
    c: Coincident(g5,g3)
    c: Equal(g3,g2)
    c: Equal(g2,g-3)
    c: Equal(g0,g1)
    c: Equal(g1,g-5)
    c: Coincident(g10,g3)
    c: Coincident(g11,g2)
    c: Coincident(g11,g8)
    c: Coincident(g12,g8)
    c: Coincident(g13,g0)
    c: Coincident(g14,g1)
    c: Coincident(g14,g6)
    c: Vertical(g14)
    c: Coincident(g15,g6)
    c: Vertical(g13)
    c: Vertical(g11)
    c: Vertical(g10)
    c: Horizontal(g12)
    c: Horizontal(g15)
    c: Equal(g14,g13)
    c: Equal(g13,g15)
    c: Equal(g15,g4)
    c: Equal(g4,g11)
    c: Equal(g11,g12)
    c: Equal(g12,g10)
    c: Equal(g3,g9)
    c: Equal(g9,g8)
    c: Equal(g8,g7)
    c: Equal(g7,g6)
    c: Tangent(g10,g9) = -1.5708
    c: Tangent(g12,g9) = 1.5708
    c: Tangent(g13,g7) = -1.5708
    c: Tangent(g15,g7) = 1.5708
FEATURE [PartDesign::Pad] Pad003
  BaseFeature = -> Pocket016
  Direction = (0,0,1)
  Length = 2.5
  Length2 = 10
  Profile = -> Sketch022
  ReferenceAxis = -> Sketch022 [N_Axis]
  Refine = true
  Suppressed = false
  Type = 0
FEATURE [Sketcher::SketchObject] Sketch023
  ArcFitTolerance = 1e-06
  AttachmentSupport = -> [XY_Plane003]
  FullyConstrained = false
  MakeInternals = false
  MapMode = 5
  sketch-geometry (74):
    g0: LineSegment [constr] StartX=23.3 StartY=57.8 StartZ=0 EndX=59.9 EndY=57.8 EndZ=0
    g1: LineSegment [constr] StartX=59.9 StartY=57.8 StartZ=0 EndX=59.9 EndY=46.05 EndZ=0
    g2: LineSegment [constr] StartX=59.9 StartY=46.05 StartZ=0 EndX=72.15 EndY=46.05 EndZ=0
    g3: LineSegment [constr] StartX=72.15 StartY=46.05 StartZ=0 EndX=72.15 EndY=35.5 EndZ=0
    g4: LineSegment [constr] StartX=72.15 StartY=35.5 StartZ=0 EndX=80.25 EndY=35.5 EndZ=0
    g5: LineSegment [constr] StartX=83.75 StartY=35.5 StartZ=0 EndX=92 EndY=35.5 EndZ=0
    g6: ArcOfCircle [constr] CenterX=82 CenterY=35.5 CenterZ=0 NormalX=0 NormalY=0 NormalZ=1 AngleXU=0 Radius=1.75 StartAngle=0 EndAngle=3.14159
    g7: LineSegment [constr] StartX=5.5 StartY=35.5 StartZ=0 EndX=5.5 EndY=53.5 EndZ=0
    g8: LineSegment [constr] StartX=5.5 StartY=53.5 StartZ=0 EndX=11 EndY=53.5 EndZ=0
    g9: LineSegment [constr] StartX=11 StartY=35.5 StartZ=0 EndX=23.3 EndY=35.5 EndZ=0
    g10: LineSegment StartX=0.05 StartY=42.7 StartZ=0 EndX=0.75 EndY=58.05 EndZ=0
    g11: LineSegment [constr] StartX=11 StartY=35.5 StartZ=0 EndX=11 EndY=53.5 EndZ=0
    g12: LineSegment StartX=20.1 StartY=71 StartZ=0 EndX=64.2 EndY=71 EndZ=0
    g13-g18: Circle [constr] x6 (B-spline internal-alignment scaffolding for g19; pole/knot coordinates omitted)
    g19: BSplineCurve PolesCount=6 KnotsCount=4 Degree=3 IsPeriodic=0
    g20-g23: GeomPoint [constr] x4 (B-spline internal-alignment scaffolding for g19; pole/knot coordinates omitted)
    g24-g27: Circle [constr] x4 (B-spline internal-alignment scaffolding for g28; pole/knot coordinates omitted)
    g28: BSplineCurve PolesCount=4 KnotsCount=2 Degree=3 IsPeriodic=0
    g29: GeomPoint [constr] X=92 Y=35.5 Z=0
    g30: GeomPoint [constr] X=64.2 Y=71 Z=0
    g31: Circle [constr] CenterX=17 CenterY=60.5 CenterZ=0 NormalX=0 NormalY=0 NormalZ=1 AngleXU=0 Radius=1.75
    g32: LineSegment [constr] StartX=23.3 StartY=35.5 StartZ=0 EndX=23.3 EndY=57.8 EndZ=0
    g33: LineSegment StartX=0.05 StartY=42.7 StartZ=0 EndX=0 EndY=35.5 EndZ=0
    g34: LineSegment [constr] StartX=0 StartY=35.5 StartZ=0 EndX=5.5 EndY=35.5 EndZ=0
    g35: LineSegment StartX=0 StartY=35.5 StartZ=0 EndX=0 EndY=0 EndZ=0
    g36: LineSegment StartX=92 StartY=35.5 StartZ=0 EndX=92 EndY=0 EndZ=0
    g37: LineSegment [constr] StartX=23.3 StartY=-57.8 StartZ=0 EndX=59.9 EndY=-57.8 EndZ=0
    g38: LineSegment [constr] StartX=59.9 StartY=-57.8 StartZ=0 EndX=59.9 EndY=-46.05 EndZ=0
    g39: LineSegment [constr] StartX=59.9 StartY=-46.05 StartZ=0 EndX=72.15 EndY=-46.05 EndZ=0
    g40: LineSegment [constr] StartX=72.15 StartY=-46.05 StartZ=0 EndX=72.15 EndY=-35.5 EndZ=0
    g41: LineSegment [constr] StartX=72.15 StartY=-35.5 StartZ=0 EndX=80.25 EndY=-35.5 EndZ=0
    g42: LineSegment [constr] StartX=83.75 StartY=-35.5 StartZ=0 EndX=92 EndY=-35.5 EndZ=0
    g43: ArcOfCircle [constr] CenterX=82 CenterY=-35.5 CenterZ=0 NormalX=0 NormalY=0 NormalZ=1 AngleXU=0 Radius=1.75 StartAngle=3.14159 EndAngle=6.28319
    g44: LineSegment [constr] StartX=5.5 StartY=-35.5 StartZ=0 EndX=5.5 EndY=-53.5 EndZ=0
    g45: LineSegment [constr] StartX=5.5 StartY=-53.5 StartZ=0 EndX=11 EndY=-53.5 EndZ=0
    g46: LineSegment [constr] StartX=11 StartY=-35.5 StartZ=0 EndX=23.3 EndY=-35.5 EndZ=0
    g47: LineSegment StartX=0.05 StartY=-42.7 StartZ=0 EndX=0.75 EndY=-58.05 EndZ=0
    g48: LineSegment [constr] StartX=11 StartY=-35.5 StartZ=0 EndX=11 EndY=-53.5 EndZ=0
    g49: LineSegment StartX=20.1 StartY=-71 StartZ=0 EndX=64.2 EndY=-71 EndZ=0
    g50-g55: Circle [constr] x6 (B-spline internal-alignment scaffolding for g56; pole/knot coordinates omitted)
    g56: BSplineCurve PolesCount=6 KnotsCount=4 Degree=3 IsPeriodic=0
    g57-g60: GeomPoint [constr] x4 (B-spline internal-alignment scaffolding for g56; pole/knot coordinates omitted)
    g61-g64: Circle [constr] x4 (B-spline internal-alignment scaffolding for g65; pole/knot coordinates omitted)
    g65: BSplineCurve PolesCount=4 KnotsCount=2 Degree=3 IsPeriodic=0
    g66: GeomPoint [constr] X=92 Y=-35.5 Z=0
    g67: GeomPoint [constr] X=64.2 Y=-71 Z=0
    g68: Circle [constr] CenterX=17 CenterY=-60.5 CenterZ=0 NormalX=0 NormalY=0 NormalZ=1 AngleXU=0 Radius=1.75
    g69: LineSegment [constr] StartX=23.3 StartY=-35.5 StartZ=0 EndX=23.3 EndY=-57.8 EndZ=0
    g70: LineSegment StartX=0.05 StartY=-42.7 StartZ=0 EndX=0 EndY=-35.5 EndZ=0
    g71: LineSegment [constr] StartX=0 StartY=-35.5 StartZ=0 EndX=5.5 EndY=-35.5 EndZ=0
    g72: LineSegment StartX=0 StartY=-35.5 StartZ=0 EndX=0 EndY=0 EndZ=0
    g73: LineSegment StartX=92 StartY=-35.5 StartZ=0 EndX=92 EndY=0 EndZ=0
  constraints (129):
    c: Horizontal(g0)
    c: Coincident(g0,g1)
    c: Vertical(g1)
    c: Coincident(g1,g2)
    c: Horizontal(g2)
    c: Coincident(g2,g3)
    c: Vertical(g3)
    c: Coincident(g4,g3)
    c: Coincident(g6,g4)
    c: Coincident(g6,g5)
    c: Vertical(g7)
    c: Horizontal(g8)
    c: DistanceX(g-1,g7) = 5.5
    c: DistanceX(g7,g9) = 5.5
    c: Coincident(g8,g7)
    c: Diameter(g6) = 3.5
    c: DistanceX(g5,g5) = 8.25
    c: DistanceX(g5) = 92
    c: DistanceX(g10) = 0.75
    c: DistanceX(g10) = 0.05
    c: Coincident(g11,g9)
    c: Coincident(g11,g8)
    c: Vertical(g11)
    c: Horizontal(g12)
    c: DistanceX(g12) = 20.1
    c: DistanceX(g12,g12) = 44.1
    c: Weight(g13) = 1
    c: Equal(g13, g14-g18) x5
    c: InternalAlignment(g13-g18 -> g19) x6
    c: InternalAlignment(g20-g23 -> g19) x4
    c: Coincident(g13,g10)
    c: Coincident(g18,g12)
    c: Weight(g24) = 1
    c: Equal(g24,g25)
    c: Equal(g24,g27)
    c: InternalAlignment(g24-g27 -> g28) x4
    c: InternalAlignment(g29,g28)
    c: InternalAlignment(g30,g28)
    c: Coincident(g24,g5)
    c: Coincident(g27,g12)
    c: DistanceX(g31,g6) = 65
    c: Equal(g31,g6)
    c: Coincident(g32,g9)
    c: Coincident(g32,g0)
    c: Vertical(g32)
    c: DistanceX(g9,g9) = 12.3
    c: DistanceY(g32,g32) = 22.3
    c: DistanceX(g0,g0) = 36.6
    c: DistanceY(g1,g1) = 11.75
    c: DistanceX(g2,g2) = 12.25
    c: DistanceX(g4,g4) = 8.1
    c: Horizontal(g7,g9)
    c: Horizontal(g9,g9)
    c: Horizontal(g9,g3)
    c: Horizontal(g3,g4)
    c: Horizontal(g4,g5)
    c: Horizontal(g5,g28)
    c: Coincident(g10,g33)
    c: Coincident(g33,g34)
    c: Coincident(g34,g7)
    c: PointOnObject(g33,g-2)
    c: Horizontal(g34)
    c: DistanceY(g7,g7) = 18
    c: DistanceY(g7,g10) = 7.2
    c: DistanceY(g7,g19) = 22.55
    c: DistanceY(g9,g31) = 25
    c: DistanceY(g9,g19) = 35.5
    c: DistanceX(g28,g25) = 0.39
    c: DistanceY(g28,g25) = 11.81
    c: DistanceY(g25,g26) = 23.27
    c: DistanceX(g26,g25) = 4.26
    c: DistanceY(g19,g14) = 1.96
    c: DistanceX(g19,g14) = 0.04043
    c: DistanceX(g14,g15) = 2.11
    c: DistanceY(g14,g15) = 3.83
    c: DistanceX(g15,g16) = 7.75
    c: DistanceY(g15,g16) = 6.89
    c: DistanceX(g16,g17) = 3.85
    c: DistanceY(g17,g16) = 0.41
    c: Horizontal(g4,g6)
    c: DistanceY(g33) = 35.5
    c: Coincident(g35,g33)
    c: Coincident(g35,g-1)
    c: Coincident(g36,g28)
    c: PointOnObject(g36,g-1)
    c: Vertical(g36)
    c: Horizontal(g37)
    c: Coincident(g37,g38)
    c: Vertical(g38)
    c: Coincident(g38,g39)
    c: Horizontal(g39)
    c: Coincident(g39,g40)
    c: Vertical(g40)
    c: Coincident(g41,g40)
    c: Coincident(g43,g41)
    c: Coincident(g43,g42)
    c: Vertical(g44)
    c: Horizontal(g45)
    c: Coincident(g45,g44)
    c: Diameter(g43) = 3.5
    c: Coincident(g48,g46)
    c: Coincident(g48,g45)
    c: Vertical(g48)
    c: Horizontal(g49)
    c: Weight(g50) = 1
    c: Equal(g50, g51-g55) x5
    c: InternalAlignment(g50-g55 -> g56) x6
    c: InternalAlignment(g57-g60 -> g56) x4
    c: Coincident(g50,g47)
    c: Coincident(g55,g49)
    c: Weight(g61) = 1
    c: Equal(g61,g62)
    c: Equal(g61,g64)
    c: InternalAlignment(g61-g64 -> g65) x4
    c: InternalAlignment(g66,g65)
    c: InternalAlignment(g67,g65)
    c: Coincident(g61,g42)
    c: Coincident(g64,g49)
    c: Equal(g68,g43)
    c: Coincident(g69,g46)
    c: Coincident(g69,g37)
    c: Vertical(g69)
    c: Coincident(g47,g70)
    c: Coincident(g70,g71)
    c: Coincident(g71,g44)
    c: Horizontal(g71)
    c: Coincident(g72,g70)
    c: Coincident(g73,g65)
    c: Vertical(g73)
FEATURE [PartDesign::Pad] Pad004
  Direction = (0,0,1)
  Length = 12
  Length2 = 10
  Profile = -> Sketch023
  ReferenceAxis = -> Sketch023 [N_Axis]
  Refine = true
  Suppressed = false
  Type = 0
FEATURE [PartDesign::Body] Body003  label="Double Bottom v2"
  AllowCompound = false
  Group = -> [Sketch023,Pad004]
  Origin = -> Origin003
  Tip = -> Pad004
FEATURE [PartDesign::Mirrored] Mirrored001
  BaseFeature = -> Pad003
  MirrorPlane = -> XZ_Plane002
  Originals = -> [Pad003]
  Refine = true
  Suppressed = false
  TransformMode = 1
FEATURE [PartDesign::Body] Body002  label="Single Bottom v2"
  AllowCompound = false
  Group = -> [Sketch016,Pad002,Sketch017,Pocket014,Sketch018,Pocket015,Sketch019,Pocket016,Sketch022,Pad003,Mirrored001]
  Origin = -> Origin002
  Placement = pos=(0,0,-12) rot=(0,0,1;0rad)
  Tip = -> Mirrored001
FEATURE [Sketcher::SketchObject] Sketch024
  ArcFitTolerance = 1e-06
  AttachmentSupport = -> [XY_Plane004]
  FullyConstrained = false
  MakeInternals = false
  MapMode = 5
  sketch-geometry (36):
    g0: LineSegment [constr] StartX=23.3 StartY=22.3 StartZ=0 EndX=59.9 EndY=22.3 EndZ=0
    g1: LineSegment [constr] StartX=59.9 StartY=22.3 StartZ=0 EndX=59.9 EndY=10.55 EndZ=0
    g2: LineSegment [constr] StartX=59.9 StartY=10.55 StartZ=0 EndX=72.15 EndY=10.55 EndZ=0
    g3: LineSegment [constr] StartX=72.15 StartY=10.55 StartZ=0 EndX=72.15 EndY=0 EndZ=0
    g4: LineSegment [constr] StartX=72.15 StartY=0 StartZ=0 EndX=80.25 EndY=2e-16 EndZ=0
    g5: LineSegment [constr] StartX=83.75 StartY=0 StartZ=0 EndX=92 EndY=0 EndZ=0
    g6: ArcOfCircle [constr] CenterX=82 CenterY=0 CenterZ=0 NormalX=0 NormalY=0 NormalZ=1 AngleXU=0 Radius=1.75 StartAngle=0 EndAngle=3.14159
    g7: LineSegment [constr] StartX=0 StartY=6.35e-14 StartZ=0 EndX=5.5 EndY=0 EndZ=0
    g8: LineSegment [constr] StartX=5.5 StartY=0 StartZ=0 EndX=5.5 EndY=18 EndZ=0
    g9: LineSegment [constr] StartX=5.5 StartY=18 StartZ=0 EndX=11 EndY=18 EndZ=0
    g10: LineSegment [constr] StartX=11 StartY=0 StartZ=0 EndX=23.3 EndY=0 EndZ=0
    g11: LineSegment StartX=0.05 StartY=7.2 StartZ=0 EndX=0.75 EndY=22.55 EndZ=0
    g12: ArcOfCircle CenterX=518.425 CenterY=0 CenterZ=0 NormalX=0 NormalY=0 NormalZ=1 AngleXU=0 Radius=518.425 StartAngle=3.1277 EndAngle=3.14159
    g13: LineSegment [constr] StartX=11 StartY=0 StartZ=0 EndX=11 EndY=18 EndZ=0
    g14: LineSegment StartX=20.1 StartY=35.5 StartZ=0 EndX=64.2 EndY=35.5 EndZ=0
    g15-g20: Circle [constr] x6 (B-spline internal-alignment scaffolding for g21; pole/knot coordinates omitted)
    g21: BSplineCurve PolesCount=6 KnotsCount=4 Degree=3 IsPeriodic=0
    g22-g25: GeomPoint [constr] x4 (B-spline internal-alignment scaffolding for g21; pole/knot coordinates omitted)
    g26-g29: Circle [constr] x4 (B-spline internal-alignment scaffolding for g30; pole/knot coordinates omitted)
    g30: BSplineCurve PolesCount=4 KnotsCount=2 Degree=3 IsPeriodic=0
    g31: GeomPoint [constr] X=92 Y=0 Z=0
    g32: GeomPoint [constr] X=64.2 Y=35.5 Z=0
    g33: Circle [constr] CenterX=17 CenterY=25 CenterZ=0 NormalX=0 NormalY=0 NormalZ=1 AngleXU=0 Radius=1.75
    g34: LineSegment [constr] StartX=23.3 StartY=0 StartZ=0 EndX=23.3 EndY=22.3 EndZ=0
    g35: LineSegment StartX=0 StartY=6.35e-14 StartZ=0 EndX=92 EndY=0 EndZ=0
  constraints (73):
    c: PointOnObject(g10,g-1)
    c: Horizontal(g0)
    c: Coincident(g0,g1)
    c: Vertical(g1)
    c: Coincident(g1,g2)
    c: Horizontal(g2)
    c: Coincident(g2,g3)
    c: PointOnObject(g3,g-1)
    c: Vertical(g3)
    c: Coincident(g4,g3)
    c: PointOnObject(g4,g-1)
    c: PointOnObject(g5,g-1)
    c: PointOnObject(g5,g-1)
    c: Coincident(g6,g4)
    c: Coincident(g6,g5)
    c: PointOnObject(g6,g-1)
    c: Coincident(g7,g-1)
    c: PointOnObject(g7,g-1)
    c: Coincident(g8,g7)
    c: Vertical(g8)
    c: Horizontal(g9)
    c: PointOnObject(g10,g-1)
    c: DistanceX(g7,g7) = 5.5
    c: DistanceX(g7,g10) = 5.5
    c: Coincident(g9,g8)
    c: DistanceY(g8,g8) = 18
    c: Diameter(g6) = 3.5
    c: DistanceX(g5,g5) = 8.25
    c: DistanceX(g5) = 92
    c: DistanceX(g11) = 0.75
    c: DistanceY(g11) = 22.55
    c: Coincident(g12,g7)
    c: Coincident(g12,g11)
    c: DistanceX(g11) = 0.05
    c: DistanceY(g11) = 7.2
    c: Perpendicular(g12,g-1)
    c: Radius(g12) = 518.425
    c: Coincident(g13,g10)
    c: Coincident(g13,g9)
    c: Vertical(g13)
    c: Horizontal(g14)
    c: DistanceY(g14) = 35.5
    c: DistanceX(g14) = 20.1
    c: DistanceX(g14,g14) = 44.1
    c: Weight(g15) = 1
    c: Equal(g15, g16-g20) x5
    c: InternalAlignment(g15-g20 -> g21) x6
    c: InternalAlignment(g22-g25 -> g21) x4
    c: Coincident(g15,g11)
    c: Coincident(g20,g14)
    c: Weight(g26) = 1
    c: Equal(g26,g27)
    c: Equal(g26,g28)
    c: Equal(g26,g29)
    c: InternalAlignment(g26-g29 -> g30) x4
    c: InternalAlignment(g31,g30)
    c: InternalAlignment(g32,g30)
    c: Coincident(g26,g5)
    c: Coincident(g29,g14)
    c: DistanceY(g33) = 25
    c: DistanceX(g33,g6) = 65
    c: Equal(g33,g6)
    c: Coincident(g34,g10)
    c: Coincident(g34,g0)
    c: Vertical(g34)
    c: DistanceX(g10,g10) = 12.3
    c: DistanceY(g34,g34) = 22.3
    c: DistanceX(g0,g0) = 36.6
    c: DistanceY(g1,g1) = 11.75
    c: DistanceX(g2,g2) = 12.25
    c: DistanceX(g4,g4) = 8.1
    c: Coincident(g35,g7)
    c: Coincident(g35,g30)
FEATURE [PartDesign::Pad] Pad005
  Direction = (0,0,1)
  Length = 12
  Length2 = 10
  Profile = -> Sketch024
  ReferenceAxis = -> Sketch024 [N_Axis]
  Refine = true
  Suppressed = false
  Type = 0
FEATURE [Sketcher::SketchObject] Sketch025
  ArcFitTolerance = 1e-06
  AttachmentSupport = -> [Pad005]
  ExternalGeometry = -> [Pad005]
  FullyConstrained = true
  MakeInternals = false
  MapMode = 5
  Placement = pos=(0,0,12) rot=(0,0,1;0rad)
  sketch-geometry (36):
    g0: ArcOfCircle CenterX=82 CenterY=0 CenterZ=0 NormalX=0 NormalY=0 NormalZ=1 AngleXU=0 Radius=2.5 StartAngle=0 EndAngle=3.14159
    g1: Circle CenterX=17 CenterY=25 CenterZ=0 NormalX=0 NormalY=0 NormalZ=1 AngleXU=0 Radius=2.5
    g2: LineSegment StartX=2 StartY=0 StartZ=0 EndX=2.57586 EndY=18.6857 EndZ=0
    g3: ArcOfCircle CenterX=82 CenterY=0 CenterZ=0 NormalX=0 NormalY=0 NormalZ=1 AngleXU=0 Radius=6 StartAngle=1.5708 EndAngle=3.14159
    g4: ArcOfCircle CenterX=85.5 CenterY=8 CenterZ=0 NormalX=0 NormalY=0 NormalZ=1 AngleXU=0 Radius=2 StartAngle=4.71239 EndAngle=6.19002
    g5: ArcOfCircle CenterX=17 CenterY=25 CenterZ=0 NormalX=0 NormalY=0 NormalZ=1 AngleXU=0 Radius=6 StartAngle=3.14159 EndAngle=6.28319
    g6: ArcOfCircle CenterX=25 CenterY=31.5 CenterZ=0 NormalX=0 NormalY=0 NormalZ=1 AngleXU=0 Radius=2 StartAngle=1.5708 EndAngle=3.14159
    g7: ArcOfCircle CenterX=9 CenterY=28 CenterZ=0 NormalX=0 NormalY=0 NormalZ=1 AngleXU=0 Radius=2 StartAngle=9e-16 EndAngle=2.29046
    g8: ArcOfCircle CenterX=17.5687 CenterY=18.2237 CenterZ=0 NormalX=0 NormalY=0 NormalZ=1 AngleXU=0 Radius=15 StartAngle=2.29046 EndAngle=3.11078
    g9: LineSegment StartX=23 StartY=25 StartZ=0 EndX=23 EndY=31.5 EndZ=0
    g10: LineSegment StartX=11 StartY=25 StartZ=0 EndX=11 EndY=28 EndZ=0
    g11: LineSegment StartX=82 StartY=6 StartZ=0 EndX=85.5 EndY=6 EndZ=0
    g12: ArcOfCircle CenterX=64.0932 CenterY=10.0002 CenterZ=0 NormalX=0 NormalY=0 NormalZ=1 AngleXU=0 Radius=23.5 StartAngle=6.19002 EndAngle=7.84944
    g13: LineSegment StartX=79.5 StartY=3e-16 StartZ=0 EndX=84.5 EndY=0 EndZ=0
    g14: LineSegment StartX=2 StartY=0 StartZ=0 EndX=16 EndY=0 EndZ=0
    g15: LineSegment StartX=16 StartY=0 StartZ=0 EndX=16 EndY=1 EndZ=0
    g16: LineSegment StartX=16 StartY=1 StartZ=0 EndX=22 EndY=1 EndZ=0
    g17: LineSegment StartX=22 StartY=1 StartZ=0 EndX=22 EndY=0 EndZ=0
    g18: LineSegment StartX=22 StartY=0 StartZ=0 EndX=76 EndY=0 EndZ=0
    g19: ArcOfCircle CenterX=25.1 CenterY=31.5 CenterZ=0 NormalX=0 NormalY=0 NormalZ=1 AngleXU=0 Radius=2 StartAngle=6e-16 EndAngle=1.5708
    g20: ArcOfCircle CenterX=29.1 CenterY=12 CenterZ=0 NormalX=0 NormalY=0 NormalZ=1 AngleXU=0 Radius=2 StartAngle=3.14159 EndAngle=4.71239
    g21: ArcOfCircle CenterX=31.1 CenterY=12 CenterZ=0 NormalX=0 NormalY=0 NormalZ=1 AngleXU=0 Radius=2 StartAngle=4.71239 EndAngle=6.28319
    g22: ArcOfCircle CenterX=35.1 CenterY=31.5 CenterZ=0 NormalX=0 NormalY=0 NormalZ=1 AngleXU=0 Radius=2 StartAngle=1.5708 EndAngle=3.14159
    g23: ArcOfCircle CenterX=49.3 CenterY=31.5 CenterZ=0 NormalX=0 NormalY=0 NormalZ=1 AngleXU=0 Radius=2 StartAngle=0 EndAngle=1.5708
    g24: ArcOfCircle CenterX=53.3 CenterY=12 CenterZ=0 NormalX=0 NormalY=0 NormalZ=1 AngleXU=0 Radius=2 StartAngle=3.14159 EndAngle=4.71239
    g25: ArcOfCircle CenterX=55.3 CenterY=12 CenterZ=0 NormalX=0 NormalY=0 NormalZ=1 AngleXU=0 Radius=2 StartAngle=4.71239 EndAngle=6.28319
    g26: ArcOfCircle CenterX=59.3 CenterY=31.5 CenterZ=0 NormalX=0 NormalY=0 NormalZ=1 AngleXU=0 Radius=2 StartAngle=1.5708 EndAngle=3.14159
    g27: LineSegment StartX=59.3 StartY=33.5 StartZ=0 EndX=64.2 EndY=33.5 EndZ=0
    g28: LineSegment StartX=57.3 StartY=31.5 StartZ=0 EndX=57.3 EndY=12 EndZ=0
    g29: LineSegment StartX=55.3 StartY=10 StartZ=0 EndX=53.3 EndY=10 EndZ=0
    g30: LineSegment StartX=51.3 StartY=12 StartZ=0 EndX=51.3 EndY=31.5 EndZ=0
    g31: LineSegment StartX=49.3 StartY=33.5 StartZ=0 EndX=35.1 EndY=33.5 EndZ=0
    g32: LineSegment StartX=33.1 StartY=31.5 StartZ=0 EndX=33.1 EndY=12 EndZ=0
    g33: LineSegment StartX=31.1 StartY=10 StartZ=0 EndX=29.1 EndY=10 EndZ=0
    g34: LineSegment StartX=27.1 StartY=12 StartZ=0 EndX=27.1 EndY=31.5 EndZ=0
    g35: LineSegment StartX=25.1 StartY=33.5 StartZ=0 EndX=25 EndY=33.5 EndZ=0
  constraints (97):
    c: PointOnObject(g0,g-1)
    c: PointOnObject(g0,g-1)
    c: PointOnObject(g0,g-1)
    c: PointOnObject(g2,g-1)
    c: DistanceX(g-1,g2) = 2
    c: Vertical(g12,g-3)
    c: DistanceY(g12,g-3) = 2
    c: Vertical(g10)
    c: Tangent(g11,g4) = -1.5708
    c: Tangent(g11,g3) = 1.5708
    c: Tangent(g9,g6) = 1.5708
    c: Tangent(g9,g5) = -1.5708
    c: Tangent(g10,g5) = 1.5708
    c: Tangent(g10,g7) = -1.5708
    c: Vertical(g9)
    c: Coincident(g5,g1)
    c: Coincident(g3,g0)
    c: Horizontal(g11)
    c: Tangent(g8,g7) = -1.5708
    c: Equal(g1,g0)
    c: Diameter(g0) = 5
    c: Tangent(g12,g4) = -1.5708
    c: Radius(g3) = 6
    c: Equal(g7,g6)
    c: Equal(g4,g6)
    c: Radius(g4) = 2
    c: Tangent(g8,g2) = 1.5708
    c: Equal(g3,g5)
    c: DistanceY(g1) = 25
    c: DistanceX(g1) = 17
    c: DistanceX(g1,g0) = 65
    c: Radius(g12) = 23.5
    c: Distance(g2,g-4) = 2
    c: Radius(g8) = 15
    c: DistanceY(g10,g10) = 3
    c: Coincident(g13,g0)
    c: Coincident(g13,g0)
    c: Coincident(g2,g14)
    c: PointOnObject(g14,g-1)
    c: Coincident(g14,g15)
    c: Coincident(g15,g16)
    c: Coincident(g16,g17)
    c: PointOnObject(g17,g-1)
    c: Vertical(g17)
    c: Coincident(g17,g18)
    c: Coincident(g18,g3)
    c: Horizontal(g18)
    c: DistanceX(g14) = 16
    c: Horizontal(g16)
    c: DistanceY(g15) = 1
    c: DistanceX(g16,g16) = 6
    c: Vertical(g15)
    c: Coincident(g27,g12)
    c: Horizontal(g31)
    c: Vertical(g32)
    c: Horizontal(g35)
    c: Tangent(g35,g6) = -1.5708
    c: Tangent(g35,g19) = -1.5708
    c: Tangent(g34,g19) = -1.5708
    c: Tangent(g34,g20) = 1.5708
    c: Tangent(g33,g20) = 1.5708
    c: Tangent(g33,g21) = 1.5708
    c: Tangent(g32,g21) = 1.5708
    c: Tangent(g32,g22) = -1.5708
    c: Tangent(g31,g22) = -1.5708
    c: Tangent(g31,g23) = -1.5708
    c: Tangent(g30,g23) = -1.5708
    c: Tangent(g30,g24) = 1.5708
    c: Tangent(g29,g24) = 1.5708
    c: Tangent(g29,g25) = 1.5708
    c: Tangent(g28,g25) = 1.5708
    c: Tangent(g27,g26) = 1.5708
    c: Tangent(g28,g26) = -1.5708
    c: Horizontal(g27)
    c: Vertical(g34)
    c: Horizontal(g33)
    c: Vertical(g30)
    c: Vertical(g28)
    c: Horizontal(g29)
    c: Horizontal(g23,g26)
    c: Horizontal(g24,g21)
    c: Equal(g25,g24)
    c: Equal(g24,g21)
    c: Equal(g21,g20)
    c: Horizontal(g19,g22)
    c: Equal(g19,g22)
    c: Equal(g22,g23)
    c: Equal(g23,g26)
    c: Equal(g6,g19)
    c: Equal(g19,g20)
    c: Equal(g33,g29)
    c: DistanceX(g35,g35) = 0.1
    c: DistanceX(g27,g27) = 4.9
    c: DistanceX(g33,g33) = 2
    c: DistanceY(g21) = 10
    c: DistanceX(g11,g11) = 3.5
    c: DistanceX(g21,g24) = 18.2
FEATURE [PartDesign::Pocket] Pocket019
  BaseFeature = -> Pad005
  Direction = (0,0,-1)
  Length = 0
  Length2 = 5
  Offset = -2
  Profile = -> Sketch025
  ReferenceAxis = -> Sketch025 [N_Axis]
  Refine = true
  Suppressed = false
  Type = 3
  UpToFace = -> Pad005 [Face7]
FEATURE [Sketcher::SketchObject] Sketch026
  ArcFitTolerance = 1e-06
  AttachmentSupport = -> [Pocket019]
  ExternalGeometry = -> [Pocket019]
  FullyConstrained = true
  MakeInternals = false
  MapMode = 5
  Placement = pos=(0,6.35e-14,0) rot=(1,0,0;1.5708rad)
  sketch-geometry (5):
    g0: LineSegment StartX=22 StartY=12 StartZ=0 EndX=22 EndY=4 EndZ=0
    g1: LineSegment StartX=22 StartY=4 StartZ=0 EndX=18 EndY=10 EndZ=0
    g2: LineSegment StartX=18 StartY=10 StartZ=0 EndX=16 EndY=10 EndZ=0
    g3: LineSegment StartX=16 StartY=10 StartZ=0 EndX=16 EndY=12 EndZ=0
    g4: LineSegment StartX=16 StartY=12 StartZ=0 EndX=22 EndY=12 EndZ=0
  constraints (13):
    c: Vertical(g0)
    c: Coincident(g0,g1)
    c: Coincident(g1,g2)
    c: Horizontal(g2)
    c: Coincident(g2,g3)
    c: Coincident(g3,g-3)
    c: Vertical(g3)
    c: Coincident(g3,g4)
    c: Coincident(g4,g-3)
    c: Coincident(g0,g4)
    c: DistanceY(g-4,g0) = 2
    c: DistanceY(g-4,g1) = 8
    c: DistanceX(g2,g2) = 2
FEATURE [PartDesign::Pocket] Pocket020
  BaseFeature = -> Pocket019
  Direction = (0,1,-2e-16)
  Length = 5
  Length2 = 5
  Profile = -> Sketch026
  ReferenceAxis = -> Sketch026 [N_Axis]
  Refine = true
  Suppressed = false
  Type = 2
FEATURE [Sketcher::SketchObject] Sketch027
  ArcFitTolerance = 1e-06
  AttachmentSupport = -> [YZ_Plane004]
  FullyConstrained = true
  MakeInternals = false
  MapMode = 5
  Placement = pos=(0,0,0) rot=(0.57735,0.57735,0.57735;2.0944rad)
  sketch-geometry (4):
    g0: LineSegment StartX=0 StartY=2 StartZ=0 EndX=8 EndY=2 EndZ=0
    g1: LineSegment StartX=8 StartY=2 StartZ=0 EndX=8 EndY=10.3 EndZ=0
    g2: LineSegment StartX=8 StartY=10.3 StartZ=0 EndX=0 EndY=10.3 EndZ=0
    g3: LineSegment StartX=0 StartY=10.3 StartZ=0 EndX=0 EndY=2 EndZ=0
  constraints (12):
    c: Coincident(g0,g1)
    c: Coincident(g1,g2)
    c: Coincident(g2,g3)
    c: Coincident(g3,g0)
    c: Horizontal(g0)
    c: Horizontal(g2)
    c: Vertical(g1)
    c: Vertical(g3)
    c: PointOnObject(g0,g-2)
    c: DistanceX(g2,g2) = 8
    c: DistanceY(g3,g3) = 8.3
    c: DistanceY(g0) = 2
FEATURE [PartDesign::Pocket] Pocket021
  BaseFeature = -> Pocket020
  Direction = (-1,0,0)
  Length = 5
  Length2 = 5
  Profile = -> Sketch027
  ReferenceAxis = -> Sketch027 [N_Axis]
  Refine = true
  Reversed = true
  Suppressed = false
  Type = 0
FEATURE [Sketcher::SketchObject] Sketch028
  ArcFitTolerance = 1e-06
  AttachmentSupport = -> [Pocket021]
  ExternalGeometry = -> [Pocket021]
  FullyConstrained = true
  MakeInternals = false
  MapMode = 5
  Placement = pos=(0,0,12) rot=(0,0,1;0rad)
  sketch-geometry (16):
    g0: ArcOfCircle CenterX=31.1 CenterY=12 CenterZ=0 NormalX=0 NormalY=0 NormalZ=1 AngleXU=0 Radius=2 StartAngle=4.71239 EndAngle=6.28319
    g1: ArcOfCircle CenterX=29.1 CenterY=12 CenterZ=0 NormalX=0 NormalY=0 NormalZ=1 AngleXU=0 Radius=2 StartAngle=3.14159 EndAngle=4.71239
    g2: ArcOfCircle CenterX=53.3 CenterY=12 CenterZ=0 NormalX=0 NormalY=0 NormalZ=1 AngleXU=0 Radius=2 StartAngle=3.14159 EndAngle=4.71239
    g3: ArcOfCircle CenterX=55.3 CenterY=12 CenterZ=0 NormalX=0 NormalY=0 NormalZ=1 AngleXU=0 Radius=2 StartAngle=4.71239 EndAngle=6.28319
    g4: LineSegment StartX=29.1 StartY=10 StartZ=0 EndX=31.1 EndY=10 EndZ=0
    g5: LineSegment StartX=53.3 StartY=10 StartZ=0 EndX=55.3 EndY=10 EndZ=0
    g6: ArcOfCircle CenterX=29.1 CenterY=14 CenterZ=0 NormalX=0 NormalY=0 NormalZ=1 AngleXU=0 Radius=2 StartAngle=1.5708 EndAngle=3.14159
    g7: ArcOfCircle CenterX=31.1 CenterY=14 CenterZ=0 NormalX=0 NormalY=0 NormalZ=1 AngleXU=0 Radius=2 StartAngle=3e-16 EndAngle=1.5708
    g8: ArcOfCircle CenterX=53.3 CenterY=14 CenterZ=0 NormalX=0 NormalY=0 NormalZ=1 AngleXU=0 Radius=2 StartAngle=1.5708 EndAngle=3.14159
    g9: ArcOfCircle CenterX=55.3 CenterY=14 CenterZ=0 NormalX=0 NormalY=0 NormalZ=1 AngleXU=0 Radius=2 StartAngle=1e-16 EndAngle=1.5708
    g10: LineSegment StartX=57.3 StartY=12 StartZ=0 EndX=57.3 EndY=14 EndZ=0
    g11: LineSegment StartX=51.3 StartY=12 StartZ=0 EndX=51.3 EndY=14 EndZ=0
    g12: LineSegment StartX=53.3 StartY=16 StartZ=0 EndX=55.3 EndY=16 EndZ=0
    g13: LineSegment StartX=33.1 StartY=12 StartZ=0 EndX=33.1 EndY=14 EndZ=0
    g14: LineSegment StartX=27.1 StartY=12 StartZ=0 EndX=27.1 EndY=14 EndZ=0
    g15: LineSegment StartX=29.1 StartY=16 StartZ=0 EndX=31.1 EndY=16 EndZ=0
  constraints (44):
    c: Coincident(g0,g-5)
    c: Coincident(g0,g-5)
    c: Coincident(g1,g-6)
    c: Coincident(g1,g-6)
    c: Coincident(g2,g-3)
    c: Coincident(g2,g-3)
    c: Coincident(g3,g-4)
    c: Coincident(g3,g-4)
    c: Coincident(g4,g1)
    c: Coincident(g4,g0)
    c: Coincident(g5,g2)
    c: Coincident(g5,g3)
    c: Equal(g3,g2)
    c: Equal(g2,g-3)
    c: Equal(g0,g1)
    c: Equal(g1,g-5)
    c: Coincident(g10,g3)
    c: Coincident(g11,g2)
    c: Coincident(g11,g8)
    c: Coincident(g12,g8)
    c: Coincident(g13,g0)
    c: Coincident(g14,g1)
    c: Coincident(g14,g6)
    c: Vertical(g14)
    c: Coincident(g15,g6)
    c: Vertical(g13)
    c: Vertical(g11)
    c: Vertical(g10)
    c: Horizontal(g12)
    c: Horizontal(g15)
    c: Equal(g14,g13)
    c: Equal(g13,g15)
    c: Equal(g15,g4)
    c: Equal(g4,g11)
    c: Equal(g11,g12)
    c: Equal(g12,g10)
    c: Equal(g3,g9)
    c: Equal(g9,g8)
    c: Equal(g8,g7)
    c: Equal(g7,g6)
    c: Tangent(g10,g9) = -1.5708
    c: Tangent(g12,g9) = 1.5708
    c: Tangent(g13,g7) = -1.5708
    c: Tangent(g15,g7) = 1.5708
FEATURE [PartDesign::Pad] Pad006
  BaseFeature = -> Pocket021
  Direction = (0,0,1)
  Length = 2.5
  Length2 = 10
  Profile = -> Sketch028
  ReferenceAxis = -> Sketch028 [N_Axis]
  Refine = true
  Suppressed = false
  Type = 0
FEATURE [PartDesign::Mirrored] Mirrored002
  BaseFeature = -> Pad006
  MirrorPlane = -> XZ_Plane004
  Originals = -> [Pad006]
  Refine = true
  Suppressed = false
  TransformMode = 1
FEATURE [Sketcher::SketchObject] Sketch029
  ArcFitTolerance = 1e-06
  AttachmentSupport = -> [Mirrored002]
  ExternalGeometry = -> [Mirrored002]
  FullyConstrained = true
  MakeInternals = false
  MapMode = 5
  Placement = pos=(0,35.5,0) rot=(0,0.707107,0.707107;3.14159rad)
  sketch-geometry (6):
    g0: LineSegment StartX=-48.9 StartY=9.5 StartZ=0 EndX=-48.9 EndY=4.5 EndZ=0
    g1: LineSegment StartX=-48.9 StartY=4.5 StartZ=0 EndX=-36.4 EndY=4.5 EndZ=0
    g2: LineSegment StartX=-36.4 StartY=4.5 StartZ=0 EndX=-36.4 EndY=9.5 EndZ=0
    g3: LineSegment StartX=-36.4 StartY=9.5 StartZ=0 EndX=-48.9 EndY=9.5 EndZ=0
    g4: GeomPoint [constr] X=-42.65 Y=7 Z=0
    g5: LineSegment [constr] StartX=-51.3 StartY=7 StartZ=0 EndX=-34 EndY=7 EndZ=0
  constraints (16):
    c: Coincident(g0,g1)
    c: Coincident(g1,g2)
    c: Coincident(g2,g3)
    c: Coincident(g3,g0)
    c: Vertical(g0)
    c: Vertical(g2)
    c: Horizontal(g1)
    c: Horizontal(g3)
    c: Symmetric(g2,g0,g4)
    c: PointOnObject(g5,g-4)
    c: PointOnObject(g5,g-5)
    c: Horizontal(g5)
    c: Symmetric(g5,g5,g4)
    c: DistanceX(g3,g3) = 12.5
    c: DistanceY(g-3,g1) = 2.5
    c: DistanceY(g0,g0) = 5
FEATURE [PartDesign::Pocket] Pocket022
  BaseFeature = -> Mirrored002
  Direction = (0,-1,2e-16)
  Length = 5
  Length2 = 5
  Profile = -> Sketch029
  ReferenceAxis = -> Sketch029 [N_Axis]
  Refine = true
  Suppressed = false
  Type = 2
FEATURE [PartDesign::Body] Body004  label="Single Bottom v2 USB"
  AllowCompound = false
  Group = -> [Sketch024,Pad005,Sketch025,Pocket019,Sketch026,Pocket020,Sketch027,Pocket021,Sketch028,Pad006,Mirrored002,Sketch029,Pocket022]
  Origin = -> Origin004
  Placement = pos=(0,0,-12) rot=(0,0,1;0rad)
  Tip = -> Pocket022
note: 2 file-system paths scrubbed to <path> (originals preserved in the JSON sidecar)
